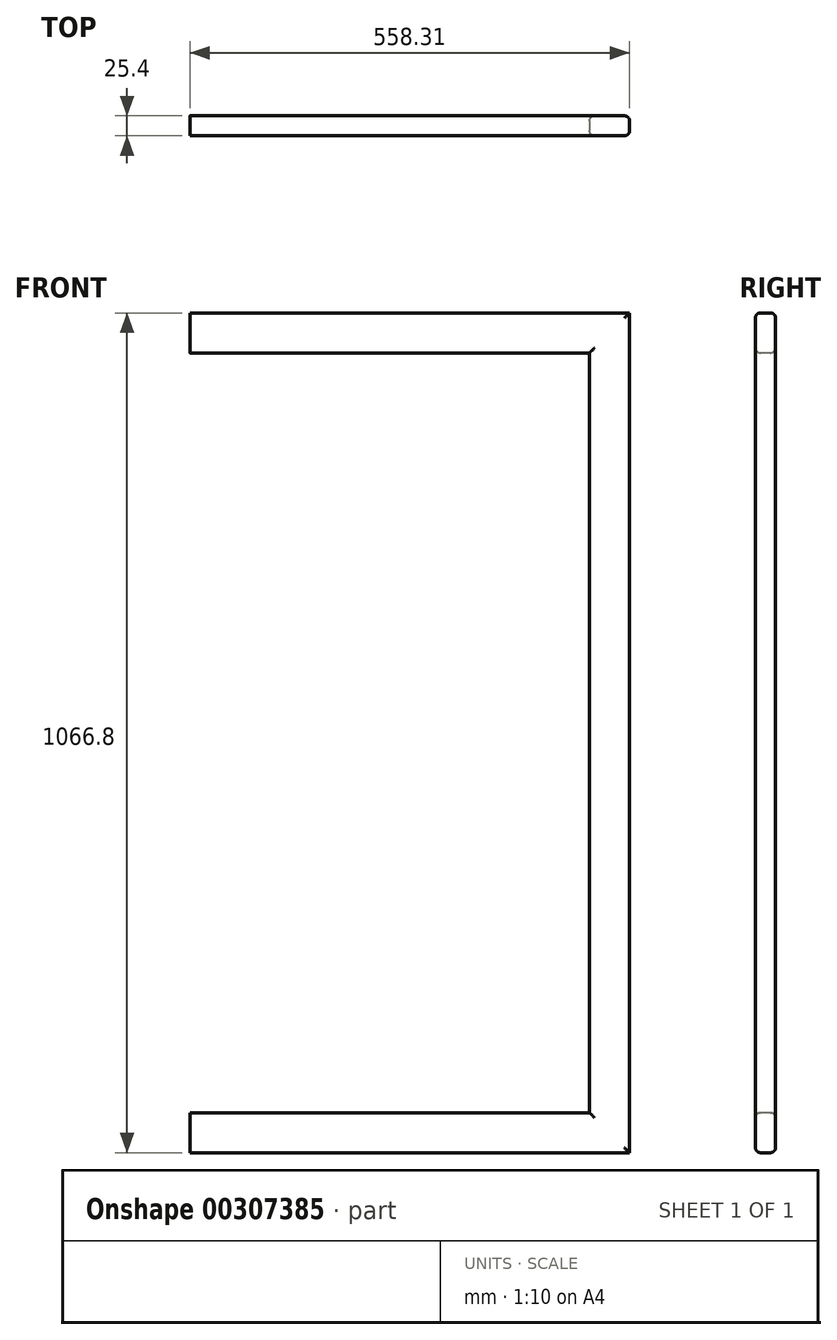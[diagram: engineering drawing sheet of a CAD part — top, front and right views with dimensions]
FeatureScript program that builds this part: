
annotation { "Feature Type Name" : "Feature", "Feature Type Description" : "" }
export const myFeature = defineFeature(function(context is Context, id is Id, definition is map)
    precondition{}
    {
        {
            var Q0;
            Q0=qCreatedBy(makeId("Front.planeOp"),FACE);
            var sketch = newSketch(context, id + "F0", { "sketchPlane" : qUnion([Q0])});
            skLineSegment(sketch, "E0", {"start": v(-2822.14, -1662.57) * mm, "end": v(-3065.65, 157.6) * mm});
            skLineSegment(sketch, "E1", {"start": v(-2797.6, -1589.77) * mm, "end": v(-3015.45, 102.14) * mm});
            skLineSegment(sketch, "E2", {"start": v(-3910.62, -1560.97) * mm, "end": v(-4015.94, -404.15) * mm});
            skLineSegment(sketch, "E3", {"start": v(-4015.94, -1560.97) * mm, "end": v(-4015.94, -404.15) * mm});
            skLineSegment(sketch, "E4", {"start": v(-4015.94, -404.15) * mm, "end": v(-4015.94, 15.92) * mm});
            skLineSegment(sketch, "E5", {"start": v(-3939.74, -1560.97) * mm, "end": v(-3939.74, -1310.71) * mm});
            skLineSegment(sketch, "E6", {"start": v(-4117.54, -1662.57) * mm, "end": v(-2823.92, -1662.57) * mm});
            skLineSegment(sketch, "E7", {"start": v(-4117.54, -1662.57) * mm, "end": v(-4117.54, 15.92) * mm});
            skLineSegment(sketch, "E8", {"start": v(-3895.3, -17.92) * mm, "end": v(-3895.3, -1662.57) * mm});
            skLineSegment(sketch, "E9", {"start": v(-3105.52, -1560.97) * mm, "end": v(-3491.84, -1560.97) * mm});
            skLineSegment(sketch, "E10", {"start": v(-2994.56, -1649.87) * mm, "end": v(-3096.16, -1649.87) * mm});
            skLineSegment(sketch, "E11", {"start": v(-2994.56, -1586.37) * mm, "end": v(-3096.16, -1586.37) * mm});
            skLineSegment(sketch, "E12", {"start": v(-4009.6, -1649.87) * mm, "end": v(-4111.2, -1649.87) * mm});
            skLineSegment(sketch, "E13", {"start": v(-4009.6, -1586.37) * mm, "end": v(-4111.2, -1586.37) * mm});
            skLineSegment(sketch, "E14", {"start": v(-4111.2, -1662.57) * mm, "end": v(-4111.2, -1586.37) * mm});
            skLineSegment(sketch, "E15", {"start": v(-4009.6, -1662.57) * mm, "end": v(-4009.6, -1586.37) * mm});
            skLineSegment(sketch, "E16", {"start": v(-2988.2, -1662.57) * mm, "end": v(-2988.2, -1560.97) * mm});
            skLineSegment(sketch, "E17", {"start": v(-2797.6, -1589.77) * mm, "end": v(-2823.92, -1662.57) * mm});
            skLineSegment(sketch, "E18", {"start": v(-4015.94, -1241.94) * mm, "end": v(-3953.21, -1241.94) * mm});
            skLineSegment(sketch, "E19", {"start": v(-2994.56, -1662.57) * mm, "end": v(-2994.56, -1586.37) * mm});
            skLineSegment(sketch, "E20", {"start": v(-3895.3, 217.03) * mm, "end": v(-3895.3, -17.92) * mm});
            skCircle(sketch, "E21", {"center": v(-4058.87, 166.23) * mm, "radius": 31.75 * mm});
            skCircle(sketch, "E22", {"center": v(-4058.87, 166.23) * mm, "radius": 26.92 * mm});
            skLineSegment(sketch, "E23", {"start": v(-3015.45, 102.14) * mm, "end": v(-3065.74, 157.9) * mm});
            skLineSegment(sketch, "E24", {"start": v(4405, 193.82) * mm, "end": v(3084.2, 193.82) * mm});
            skLineSegment(sketch, "E25", {"start": v(3085.2, -1658.86) * mm, "end": v(4405, -1658.86) * mm});
            skLineSegment(sketch, "E26", {"start": v(3084.2, -1654.29) * mm, "end": v(4405, -1654.29) * mm});
            skLineSegment(sketch, "E27", {"start": v(3004.35, -1658.98) * mm, "end": v(3004.35, 220.62) * mm});
            skLineSegment(sketch, "E28", {"start": v(3038.49, -1589.93) * mm, "end": v(3038.49, 154.88) * mm});
            skLineSegment(sketch, "E29", {"start": v(3041.54, -1586.18) * mm, "end": v(3041.54, 155.86) * mm});
            skLineSegment(sketch, "E30", {"start": v(3084.2, -1654.29) * mm, "end": v(3041.54, -1586.18) * mm});
            skLineSegment(sketch, "E31", {"start": v(3079.81, -1655.88) * mm, "end": v(3037.66, -1588.6) * mm});
            skLineSegment(sketch, "E32", {"start": v(2985.3, -1646.28) * mm, "end": v(2909.1, -1646.28) * mm});
            skArc(sketch, "E33", {"start": v(2909.1, -1646.28) * mm, "mid": v(2904.6, -1648.14) * mm, "end": v(2902.75, -1652.63) * mm});
            skLineSegment(sketch, "E34", {"start": v(2902.75, -1658.98) * mm, "end": v(2902.75, -1652.63) * mm});
            skLineSegment(sketch, "E35", {"start": v(3043.97, -1658.98) * mm, "end": v(3043.97, -1598.68) * mm});
            skLineSegment(sketch, "E36", {"start": v(3041.54, -1658.86) * mm, "end": v(3041.54, -1594.8) * mm});
            skLineSegment(sketch, "E37", {"start": v(3004.35, -1582.78) * mm, "end": v(2998, -1582.78) * mm});
            skLineSegment(sketch, "E38", {"start": v(2991.65, -1639.93) * mm, "end": v(2991.65, -1589.13) * mm});
            skArc(sketch, "E39", {"start": v(2998, -1582.78) * mm, "mid": v(2993.5, -1584.64) * mm, "end": v(2991.65, -1589.13) * mm});
            skArc(sketch, "E40", {"start": v(2985.3, -1646.28) * mm, "mid": v(2989.79, -1644.42) * mm, "end": v(2991.65, -1639.93) * mm});
            skLineSegment(sketch, "E41", {"start": v(3043.97, -1617.83) * mm, "end": v(3055.97, -1617.83) * mm});
            skLineSegment(sketch, "E42", {"start": v(3038.49, -1586.18) * mm, "end": v(3041.54, -1586.18) * mm});
            skArc(sketch, "E43", {"start": v(3079.81, -1655.88) * mm, "mid": v(3082.12, -1658.07) * mm, "end": v(3085.2, -1658.86) * mm});
            skLineSegment(sketch, "E44", {"start": v(3068.03, 201.69) * mm, "end": v(3046.1, 201.69) * mm});
            skLineSegment(sketch, "E45", {"start": v(3084.2, 220.74) * mm, "end": v(3041.54, 155.86) * mm});
            skLineSegment(sketch, "E46", {"start": v(3081.66, 222.41) * mm, "end": v(3039.53, 158.37) * mm});
            skLineSegment(sketch, "E47", {"start": v(3007.4, 220.62) * mm, "end": v(3007.4, 223.92) * mm});
            skLineSegment(sketch, "E48", {"start": v(3047.27, 170.13) * mm, "end": v(3047.27, 220.62) * mm});
            skLineSegment(sketch, "E49", {"start": v(3043.97, 220.62) * mm, "end": v(3043.97, 166.3) * mm});
            skArc(sketch, "E50", {"start": v(3039.53, 158.37) * mm, "mid": v(3038.75, 156.7) * mm, "end": v(3038.49, 154.88) * mm});
            skLineSegment(sketch, "E51", {"start": v(3007.4, 223.92) * mm, "end": v(3043.97, 223.92) * mm});
            skLineSegment(sketch, "E52", {"start": v(3004.35, 220.62) * mm, "end": v(3043.97, 220.62) * mm});
            skArc(sketch, "E53", {"start": v(3047.27, 220.62) * mm, "mid": v(3046.3, 222.96) * mm, "end": v(3043.97, 223.92) * mm});
            skLineSegment(sketch, "E54", {"start": v(4409.58, 220.74) * mm, "end": v(3079.64, 220.74) * mm});
            skLineSegment(sketch, "E55", {"start": v(4490, -1658.98) * mm, "end": v(4490, 220.62) * mm});
            skLineSegment(sketch, "E56", {"start": v(4405, -1658.86) * mm, "end": v(4405, 352.31) * mm});
            skLineSegment(sketch, "E57", {"start": v(4447.68, -1586.18) * mm, "end": v(4447.68, 155.86) * mm});
            skLineSegment(sketch, "E58", {"start": v(4450.73, -1589.93) * mm, "end": v(4450.73, 154.88) * mm});
            skLineSegment(sketch, "E59", {"start": v(4409.4, -1655.88) * mm, "end": v(4451.55, -1588.6) * mm});
            skLineSegment(sketch, "E60", {"start": v(4405, -1654.29) * mm, "end": v(4447.68, -1586.18) * mm});
            skLineSegment(sketch, "E61", {"start": v(4447.68, -1658.86) * mm, "end": v(4447.68, -1594.8) * mm});
            skLineSegment(sketch, "E62", {"start": v(4445.24, -1658.98) * mm, "end": v(4445.24, -1598.68) * mm});
            skArc(sketch, "E63", {"start": v(4404.02, -1658.86) * mm, "mid": v(4407.1, -1658.07) * mm, "end": v(4409.4, -1655.88) * mm});
            skLineSegment(sketch, "E64", {"start": v(4450.73, -1586.18) * mm, "end": v(4447.68, -1586.18) * mm});
            skLineSegment(sketch, "E65", {"start": v(4445.24, -1617.83) * mm, "end": v(4433.25, -1617.83) * mm});
            skLineSegment(sketch, "E66", {"start": v(4556.6, -1692.31) * mm, "end": v(4620.6, -1806.17) * mm});
            skArc(sketch, "E67", {"start": v(4588.54, -1652.63) * mm, "mid": v(4586.68, -1648.14) * mm, "end": v(4582.2, -1646.28) * mm});
            skLineSegment(sketch, "E68", {"start": v(4506, -1646.28) * mm, "end": v(4582.2, -1646.28) * mm});
            skArc(sketch, "E69", {"start": v(4499.64, -1639.93) * mm, "mid": v(4501.5, -1644.42) * mm, "end": v(4506, -1646.28) * mm});
            skArc(sketch, "E70", {"start": v(4499.64, -1589.13) * mm, "mid": v(4497.78, -1584.64) * mm, "end": v(4493.3, -1582.78) * mm});
            skLineSegment(sketch, "E71", {"start": v(4499.64, -1639.93) * mm, "end": v(4499.64, -1589.13) * mm});
            skLineSegment(sketch, "E72", {"start": v(4486.94, -1582.78) * mm, "end": v(4493.3, -1582.78) * mm});
            skLineSegment(sketch, "E73", {"start": v(4588.54, -1658.98) * mm, "end": v(4588.54, -1652.63) * mm});
            skLineSegment(sketch, "E74", {"start": v(4490, 220.62) * mm, "end": v(4447.32, 220.62) * mm});
            skLineSegment(sketch, "E75", {"start": v(4486.94, 223.92) * mm, "end": v(4447.07, 223.92) * mm});
            skLineSegment(sketch, "E76", {"start": v(4445.24, 220.62) * mm, "end": v(4445.24, 166.3) * mm});
            skLineSegment(sketch, "E77", {"start": v(4407.55, 222.41) * mm, "end": v(4449.68, 158.37) * mm});
            skLineSegment(sketch, "E78", {"start": v(4405, 220.74) * mm, "end": v(4447.68, 155.86) * mm});
            skLineSegment(sketch, "E79", {"start": v(4441.94, 170.13) * mm, "end": v(4441.94, 220.62) * mm});
            skArc(sketch, "E80", {"start": v(4450.73, 154.88) * mm, "mid": v(4450.46, 156.7) * mm, "end": v(4449.68, 158.37) * mm});
            skLineSegment(sketch, "E81", {"start": v(4421.19, 201.69) * mm, "end": v(4443.1, 201.69) * mm});
            skArc(sketch, "E82", {"start": v(4445.24, 223.92) * mm, "mid": v(4442.9, 222.96) * mm, "end": v(4441.94, 220.62) * mm});
            skLineSegment(sketch, "E83", {"start": v(4486.94, 220.62) * mm, "end": v(4486.94, 223.92) * mm});
            skLineSegment(sketch, "E84", {"start": v(1268.38, 2115.98) * mm, "end": v(1268.38, 2338.23) * mm});
            skLineSegment(sketch, "E85", {"start": v(4.47, 2115.98) * mm, "end": v(4.47, 2338.23) * mm});
            skLineSegment(sketch, "E86", {"start": v(1391.64, 1119.03) * mm, "end": v(1391.64, 2338.23) * mm});
            skLineSegment(sketch, "E87", {"start": v(1349.33, 1119.03) * mm, "end": v(1349.33, 2338.23) * mm});
            skLineSegment(sketch, "E88", {"start": v(-36.67, 2115.98) * mm, "end": v(1309.53, 2115.98) * mm});
            skLineSegment(sketch, "E89", {"start": v(-76.48, 1119.03) * mm, "end": v(-76.48, 2338.23) * mm});
            skLineSegment(sketch, "E90", {"start": v(-119.4, 1119.03) * mm, "end": v(-119.4, 2338.23) * mm});
            skLineSegment(sketch, "E91", {"start": v(1309.53, 985.68) * mm, "end": v(1309.53, 2338.23) * mm});
            skLineSegment(sketch, "E92", {"start": v(-36.67, 985.68) * mm, "end": v(-36.67, 2338.23) * mm});
            skLineSegment(sketch, "E93", {"start": v(-36.67, 985.68) * mm, "end": v(1309.53, 985.68) * mm});
            skLineSegment(sketch, "E94", {"start": v(-132.1, 1125.38) * mm, "end": v(-132.1, 1226.98) * mm});
            skLineSegment(sketch, "E95", {"start": v(-119.4, 1119.03) * mm, "end": v(-76.48, 1119.03) * mm});
            skLineSegment(sketch, "E96", {"start": v(-119.4, 1125.38) * mm, "end": v(-221, 1125.38) * mm});
            skCircle(sketch, "E97", {"center": v(-176.55, 1176.18) * mm, "radius": 6.86 * mm});
            skLineSegment(sketch, "E98", {"start": v(-221, 1226.98) * mm, "end": v(-119.4, 1226.98) * mm});
            skLineSegment(sketch, "E99", {"start": v(1349.33, 1119.03) * mm, "end": v(1391.64, 1119.03) * mm});
            skLineSegment(sketch, "E100", {"start": v(-75.54, 2255.68) * mm, "end": v(-75.54, 2319.18) * mm});
            skLineSegment(sketch, "E101", {"start": v(43.34, 2255.68) * mm, "end": v(43.34, 2319.18) * mm});
            skLineSegment(sketch, "E102", {"start": v(1268.38, 2236.63) * mm, "end": v(4.47, 2236.63) * mm});
            skLineSegment(sketch, "E103", {"start": v(43.34, 2262.03) * mm, "end": v(1229.52, 2262.03) * mm});
            skLineSegment(sketch, "E104", {"start": v(43.34, 2312.83) * mm, "end": v(1229.52, 2312.83) * mm});
            skLineSegment(sketch, "E105", {"start": v(-75.54, 2262.03) * mm, "end": v(-115.6, 2262.03) * mm});
            skLineSegment(sketch, "E106", {"start": v(-119.4, 2338.23) * mm, "end": v(1391.64, 2338.23) * mm});
            skArc(sketch, "E107", {"start": v(-115.6, 2250.19) * mm, "mid": v(-114.23, 2246.25) * mm, "end": v(-110.72, 2244.01) * mm});
            skLineSegment(sketch, "E108", {"start": v(-115.6, 2250.26) * mm, "end": v(-115.6, 2324.68) * mm});
            skLineSegment(sketch, "E109", {"start": v(-78.26, 2240.44) * mm, "end": v(-110.72, 2244.01) * mm});
            skLineSegment(sketch, "E110", {"start": v(-119.4, 2236.63) * mm, "end": v(-36.67, 2236.63) * mm});
            skLineSegment(sketch, "E111", {"start": v(-36.67, 2255.68) * mm, "end": v(-75.54, 2255.68) * mm});
            skLineSegment(sketch, "E112", {"start": v(43.34, 2255.68) * mm, "end": v(4.47, 2255.68) * mm});
            skLineSegment(sketch, "E113", {"start": v(-75.54, 2312.83) * mm, "end": v(-115.6, 2312.83) * mm});
            skLineSegment(sketch, "E114", {"start": v(-78.26, 2334.42) * mm, "end": v(-110.72, 2330.86) * mm});
            skLineSegment(sketch, "E115", {"start": v(-78.26, 2338.23) * mm, "end": v(-119.4, 2338.23) * mm});
            skArc(sketch, "E116", {"start": v(-110.72, 2330.86) * mm, "mid": v(-114.23, 2328.62) * mm, "end": v(-115.6, 2324.68) * mm});
            skLineSegment(sketch, "E117", {"start": v(-36.67, 2319.18) * mm, "end": v(-75.54, 2319.18) * mm});
            skLineSegment(sketch, "E118", {"start": v(43.34, 2319.18) * mm, "end": v(4.47, 2319.18) * mm});
            skLineSegment(sketch, "E119", {"start": v(1348.39, 2262.03) * mm, "end": v(1388.44, 2262.03) * mm});
            skLineSegment(sketch, "E120", {"start": v(1348.39, 2312.83) * mm, "end": v(1388.44, 2312.83) * mm});
            skLineSegment(sketch, "E121", {"start": v(1349.33, 2236.63) * mm, "end": v(1391.64, 2236.63) * mm});
            skLineSegment(sketch, "E122", {"start": v(1351.1, 2240.44) * mm, "end": v(1383.57, 2244.01) * mm});
            skLineSegment(sketch, "E123", {"start": v(1351.1, 2334.42) * mm, "end": v(1383.57, 2330.86) * mm});
            skLineSegment(sketch, "E124", {"start": v(1348.39, 2255.68) * mm, "end": v(1348.39, 2319.18) * mm});
            skLineSegment(sketch, "E125", {"start": v(1229.52, 2255.68) * mm, "end": v(1229.52, 2319.18) * mm});
            skLineSegment(sketch, "E126", {"start": v(1229.52, 2255.68) * mm, "end": v(1268.38, 2255.68) * mm});
            skLineSegment(sketch, "E127", {"start": v(1349.33, 2236.63) * mm, "end": v(1309.53, 2236.63) * mm});
            skLineSegment(sketch, "E128", {"start": v(1309.53, 2255.68) * mm, "end": v(1348.39, 2255.68) * mm});
            skLineSegment(sketch, "E129", {"start": v(1229.52, 2319.18) * mm, "end": v(1268.38, 2319.18) * mm});
            skLineSegment(sketch, "E130", {"start": v(1309.53, 2319.18) * mm, "end": v(1348.39, 2319.18) * mm});
            skLineSegment(sketch, "E131", {"start": v(1388.44, 2250.26) * mm, "end": v(1388.44, 2324.68) * mm});
            skArc(sketch, "E132", {"start": v(1383.57, 2244.01) * mm, "mid": v(1387.08, 2246.25) * mm, "end": v(1388.44, 2250.19) * mm});
            skArc(sketch, "E133", {"start": v(1388.44, 2324.68) * mm, "mid": v(1387.08, 2328.62) * mm, "end": v(1383.57, 2330.86) * mm});
            skLineSegment(sketch, "E134", {"start": v(1467.84, 2325.63) * mm, "end": v(1467.84, 2224.03) * mm});
            skLineSegment(sketch, "E135", {"start": v(1404.34, 2325.63) * mm, "end": v(1404.34, 2224.03) * mm});
            skLineSegment(sketch, "E136", {"start": v(1391.64, 2224.03) * mm, "end": v(1391.64, 2325.63) * mm});
            skLineSegment(sketch, "E137", {"start": v(1391.64, 2325.63) * mm, "end": v(1467.84, 2325.63) * mm});
            skLineSegment(sketch, "E138", {"start": v(-123.35, 2335.19) * mm, "end": v(-123.35, 2125.64) * mm});
            skCircle(sketch, "E139", {"center": v(1436.1, 2274.83) * mm, "radius": 6.86 * mm});
            skLineSegment(sketch, "E140", {"start": v(1467.84, 2224.03) * mm, "end": v(1391.64, 2224.03) * mm});
            skLineSegment(sketch, "E141", {"start": v(-221, 1226.98) * mm, "end": v(-221, 1125.38) * mm});
            skLineSegment(sketch, "E142", {"start": v(1392.25, 1226.98) * mm, "end": v(1392.25, 1125.38) * mm});
            skLineSegment(sketch, "E143", {"start": v(1404.95, 1125.38) * mm, "end": v(1404.95, 1226.98) * mm});
            skLineSegment(sketch, "E144", {"start": v(1493.85, 1125.38) * mm, "end": v(1493.85, 1226.98) * mm});
            skLineSegment(sketch, "E145", {"start": v(1392.25, 1125.38) * mm, "end": v(1493.85, 1125.38) * mm});
            skCircle(sketch, "E146", {"center": v(1449.4, 1176.18) * mm, "radius": 6.86 * mm});
            skLineSegment(sketch, "E147", {"start": v(1493.85, 1226.98) * mm, "end": v(1392.25, 1226.98) * mm});
            skLineSegment(sketch, "E148", {"start": v(1493.85, 1226.98) * mm, "end": v(1493.85, 1125.38) * mm});
            skLineSegment(sketch, "E149", {"start": v(3084.2, 352.31) * mm, "end": v(4405, 352.31) * mm});
            skLineSegment(sketch, "E150", {"start": v(3084.2, -1658.86) * mm, "end": v(3084.2, 352.31) * mm});
            skLineSegment(sketch, "E151", {"start": v(-3930.07, 217.03) * mm, "end": v(-3983.26, 217.03) * mm});
            skLineSegment(sketch, "E152", {"start": v(-3895.3, 344.03) * mm, "end": v(-3895.3, 217.03) * mm});
            skLineSegment(sketch, "E153", {"start": v(-3890.72, 344.03) * mm, "end": v(-3415.64, 344.03) * mm});
            skLineSegment(sketch, "E154", {"start": v(-3083.2, 214.13) * mm, "end": v(-3308.19, 344.03) * mm});
            skLineSegment(sketch, "E155", {"start": v(-3083.2, 214.13) * mm, "end": v(-3065.65, 157.6) * mm});
            skLineSegment(sketch, "E156", {"start": v(-36.67, 1223.6) * mm, "end": v(-72.6, 1187.67) * mm});
            skLineSegment(sketch, "E157", {"start": v(-72.6, 1187.67) * mm, "end": v(-72.6, 1004.21) * mm});
            skLineSegment(sketch, "E158", {"start": v(-72.6, 1004.21) * mm, "end": v(-36.67, 985.68) * mm});
            skLineSegment(sketch, "E159", {"start": v(1309.53, 1223.6) * mm, "end": v(1345.45, 1187.67) * mm});
            skLineSegment(sketch, "E160", {"start": v(1345.45, 1187.67) * mm, "end": v(1345.45, 1004.21) * mm});
            skLineSegment(sketch, "E161", {"start": v(1345.45, 1004.21) * mm, "end": v(1309.53, 985.68) * mm});
            skArc(sketch, "E162", {"start": v(-2823.92, -1662.57) * mm, "mid": v(-1901.54, 614.6) * mm, "end": v(-3652.4, 2338.2) * mm});
            skCircle(sketch, "E163", {"center": v(-3126.94, 115.43) * mm, "radius": 7.5 * mm});
            skCircle(sketch, "E164", {"center": v(-3126.94, 64.63) * mm, "radius": 7.5 * mm});
            skCircle(sketch, "E165", {"center": v(-3126.94, 13.83) * mm, "radius": 7.5 * mm});
            skCircle(sketch, "E166", {"center": v(-3126.94, -36.97) * mm, "radius": 7.5 * mm});
            skCircle(sketch, "E167", {"center": v(-3126.94, -87.77) * mm, "radius": 7.5 * mm});
            skCircle(sketch, "E168", {"center": v(-3126.94, -240.17) * mm, "radius": 7.5 * mm});
            skCircle(sketch, "E169", {"center": v(-3126.94, -189.37) * mm, "radius": 7.5 * mm});
            skCircle(sketch, "E170", {"center": v(-3126.94, -138.57) * mm, "radius": 7.5 * mm});
            skLineSegment(sketch, "E171", {"start": v(-123.35, 2335.19) * mm, "end": v(-123.35, 1823.88) * mm});
            skLineSegment(sketch, "E172", {"start": v(-123.35, 2125.64) * mm, "end": v(-119.4, 2125.64) * mm});
            skLineSegment(sketch, "E173", {"start": v(-123.35, 2335.19) * mm, "end": v(-119.4, 2335.19) * mm});
            skLineSegment(sketch, "E174", {"start": v(-197.73, -345.12) * mm, "end": v(-273.93, -345.12) * mm});
            skArc(sketch, "E175", {"start": v(-273.93, -345.12) * mm, "mid": v(-276.27, -344.16) * mm, "end": v(-277.23, -341.82) * mm});
            skLineSegment(sketch, "E176", {"start": v(-277.23, -341.82) * mm, "end": v(-277.23, -265.62) * mm});
            skArc(sketch, "E177", {"start": v(-277.23, -265.62) * mm, "mid": v(-276.27, -263.29) * mm, "end": v(-273.93, -262.32) * mm});
            skLineSegment(sketch, "E178", {"start": v(-273.93, -262.32) * mm, "end": v(-197.73, -262.32) * mm});
            skLineSegment(sketch, "E179", {"start": v(-197.73, -262.32) * mm, "end": v(-197.73, -265.62) * mm});
            skLineSegment(sketch, "E180", {"start": v(-197.73, -265.62) * mm, "end": v(-273.93, -265.62) * mm});
            skLineSegment(sketch, "E181", {"start": v(-273.93, -265.62) * mm, "end": v(-273.93, -341.82) * mm});
            skLineSegment(sketch, "E182", {"start": v(-273.93, -341.82) * mm, "end": v(-197.73, -341.82) * mm});
            skLineSegment(sketch, "E183", {"start": v(-197.73, -341.82) * mm, "end": v(-197.73, -345.12) * mm});
            skLineSegment(sketch, "E184", {"start": v(-175.63, -341.82) * mm, "end": v(-175.63, -265.62) * mm});
            skArc(sketch, "E185", {"start": v(-175.63, -265.62) * mm, "mid": v(-177.5, -261.13) * mm, "end": v(-181.98, -259.27) * mm});
            skLineSegment(sketch, "E186", {"start": v(-181.98, -259.27) * mm, "end": v(-328.03, -259.27) * mm});
            skArc(sketch, "E187", {"start": v(-328.03, -259.27) * mm, "mid": v(-332.52, -261.13) * mm, "end": v(-334.38, -265.62) * mm});
            skLineSegment(sketch, "E188", {"start": v(-334.38, -265.62) * mm, "end": v(-334.38, -341.82) * mm});
            skCircle(sketch, "E189", {"center": v(-197.86, -303.72) * mm, "radius": 7.11 * mm});
            skCircle(sketch, "E190", {"center": v(-312.16, -303.72) * mm, "radius": 7.11 * mm});
            skArc(sketch, "E191", {"start": v(-181.98, -348.17) * mm, "mid": v(-177.5, -346.31) * mm, "end": v(-175.63, -341.82) * mm});
            skLineSegment(sketch, "E192", {"start": v(-181.98, -348.17) * mm, "end": v(-328.03, -348.17) * mm});
            skArc(sketch, "E193", {"start": v(-334.38, -341.82) * mm, "mid": v(-332.52, -346.31) * mm, "end": v(-328.03, -348.17) * mm});
            skLineSegment(sketch, "E194", {"start": v(-223.13, -262.32) * mm, "end": v(-197.73, -262.32) * mm});
            skLineSegment(sketch, "E195", {"start": v(-197.73, -262.32) * mm, "end": v(-197.73, 1820.48) * mm});
            skLineSegment(sketch, "E196", {"start": v(-197.73, 1820.48) * mm, "end": v(-223.13, 1820.48) * mm});
            skLineSegment(sketch, "E197", {"start": v(-223.13, 1820.48) * mm, "end": v(-223.13, -262.32) * mm});
            skLineSegment(sketch, "E198", {"start": v(-223.13, 1823.88) * mm, "end": v(-123.35, 1823.88) * mm});
            skLineSegment(sketch, "E199", {"start": v(-197.73, 1820.48) * mm, "end": v(-119.4, 1820.48) * mm});
            skLineSegment(sketch, "E200", {"start": v(1469.97, -345.12) * mm, "end": v(1546.17, -345.12) * mm});
            skArc(sketch, "E201", {"start": v(1546.17, -345.12) * mm, "mid": v(1548.5, -344.16) * mm, "end": v(1549.47, -341.82) * mm});
            skLineSegment(sketch, "E202", {"start": v(1549.47, -341.82) * mm, "end": v(1549.47, -265.62) * mm});
            skArc(sketch, "E203", {"start": v(1549.47, -265.62) * mm, "mid": v(1548.5, -263.29) * mm, "end": v(1546.17, -262.32) * mm});
            skLineSegment(sketch, "E204", {"start": v(1546.17, -262.32) * mm, "end": v(1469.97, -262.32) * mm});
            skLineSegment(sketch, "E205", {"start": v(1469.97, -262.32) * mm, "end": v(1469.97, -265.62) * mm});
            skLineSegment(sketch, "E206", {"start": v(1469.97, -265.62) * mm, "end": v(1546.17, -265.62) * mm});
            skLineSegment(sketch, "E207", {"start": v(1546.17, -265.62) * mm, "end": v(1546.17, -341.82) * mm});
            skLineSegment(sketch, "E208", {"start": v(1546.17, -341.82) * mm, "end": v(1469.97, -341.82) * mm});
            skLineSegment(sketch, "E209", {"start": v(1469.97, -341.82) * mm, "end": v(1469.97, -345.12) * mm});
            skLineSegment(sketch, "E210", {"start": v(1447.87, -341.82) * mm, "end": v(1447.87, -265.62) * mm});
            skArc(sketch, "E211", {"start": v(1454.22, -259.27) * mm, "mid": v(1449.73, -261.13) * mm, "end": v(1447.87, -265.62) * mm});
            skLineSegment(sketch, "E212", {"start": v(1454.22, -259.27) * mm, "end": v(1600.27, -259.27) * mm});
            skArc(sketch, "E213", {"start": v(1606.62, -265.62) * mm, "mid": v(1604.76, -261.13) * mm, "end": v(1600.27, -259.27) * mm});
            skLineSegment(sketch, "E214", {"start": v(1606.62, -265.62) * mm, "end": v(1606.62, -341.82) * mm});
            skCircle(sketch, "E215", {"center": v(1470.1, -303.72) * mm, "radius": 7.11 * mm});
            skCircle(sketch, "E216", {"center": v(1584.4, -303.72) * mm, "radius": 7.11 * mm});
            skArc(sketch, "E217", {"start": v(1447.87, -341.82) * mm, "mid": v(1449.73, -346.31) * mm, "end": v(1454.22, -348.17) * mm});
            skLineSegment(sketch, "E218", {"start": v(1454.22, -348.17) * mm, "end": v(1600.27, -348.17) * mm});
            skArc(sketch, "E219", {"start": v(1600.27, -348.17) * mm, "mid": v(1604.76, -346.31) * mm, "end": v(1606.62, -341.82) * mm});
            skLineSegment(sketch, "E220", {"start": v(1495.37, -262.32) * mm, "end": v(1469.97, -262.32) * mm});
            skLineSegment(sketch, "E221", {"start": v(1469.97, -262.32) * mm, "end": v(1469.97, 1820.48) * mm});
            skLineSegment(sketch, "E222", {"start": v(1469.97, 1820.48) * mm, "end": v(1495.37, 1820.48) * mm});
            skLineSegment(sketch, "E223", {"start": v(1495.37, 1820.48) * mm, "end": v(1495.37, -262.32) * mm});
            skLineSegment(sketch, "E224", {"start": v(1495.37, 1823.88) * mm, "end": v(1393.77, 1823.88) * mm});
            skLineSegment(sketch, "E225", {"start": v(1469.97, 1820.48) * mm, "end": v(1391.64, 1820.48) * mm});
            skLineSegment(sketch, "E226", {"start": v(1393.77, 1823.88) * mm, "end": v(1393.77, 2338.23) * mm});
            skLineSegment(sketch, "E227", {"start": v(-191.66, -345.12) * mm, "end": v(1466.92, -345.12) * mm});
            skLineSegment(sketch, "E228", {"start": v(1466.92, -345.12) * mm, "end": v(1466.92, -319.72) * mm});
            skLineSegment(sketch, "E229", {"start": v(1466.92, -319.72) * mm, "end": v(-191.66, -319.72) * mm});
            skLineSegment(sketch, "E230", {"start": v(-191.66, -319.72) * mm, "end": v(-191.66, -345.12) * mm});
            skLineSegment(sketch, "E231", {"start": v(1469.97, -1981.35) * mm, "end": v(1469.97, -348.17) * mm});
            skLineSegment(sketch, "E232", {"start": v(1469.97, -348.17) * mm, "end": v(1495.37, -348.17) * mm});
            skLineSegment(sketch, "E233", {"start": v(1495.37, -348.17) * mm, "end": v(1495.37, -1981.35) * mm});
            skLineSegment(sketch, "E234", {"start": v(1495.37, -1981.35) * mm, "end": v(1469.97, -1981.35) * mm});
            skArc(sketch, "E235", {"start": v(-191.4, -319.72) * mm, "mid": v(289.32, -1500.37) * mm, "end": v(1469.97, -1981.1) * mm});
            skLineSegment(sketch, "E236", {"start": v(-195.6, 2325.63) * mm, "end": v(-195.6, 2224.03) * mm});
            skLineSegment(sketch, "E237", {"start": v(-132.1, 2325.63) * mm, "end": v(-132.1, 2224.03) * mm});
            skLineSegment(sketch, "E238", {"start": v(-119.4, 2325.63) * mm, "end": v(-195.6, 2325.63) * mm});
            skCircle(sketch, "E239", {"center": v(-163.85, 2274.83) * mm, "radius": 6.86 * mm});
            skLineSegment(sketch, "E240", {"start": v(-195.6, 2224.03) * mm, "end": v(-119.4, 2224.03) * mm});
            skLineSegment(sketch, "E241", {"start": v(-4123.95, 237.68) * mm, "end": v(-3991.34, 237.68) * mm});
            skLineSegment(sketch, "E242", {"start": v(-4130.3, -17.93) * mm, "end": v(-4130.3, 231.33) * mm});
            skArc(sketch, "E243", {"start": v(-4123.95, 237.68) * mm, "mid": v(-4128.44, 235.82) * mm, "end": v(-4130.3, 231.33) * mm});
            skArc(sketch, "E244", {"start": v(-3985.47, 233.74) * mm, "mid": v(-3987.8, 236.6) * mm, "end": v(-3991.34, 237.68) * mm});
            skCircle(sketch, "E245", {"center": v(-4003.3, 110.67) * mm, "radius": 7.5 * mm});
            skCircle(sketch, "E246", {"center": v(-4003.3, 221.8) * mm, "radius": 7.5 * mm});
            skCircle(sketch, "E247", {"center": v(-4114.43, 110.67) * mm, "radius": 7.5 * mm});
            skCircle(sketch, "E248", {"center": v(-4114.43, 221.8) * mm, "radius": 7.5 * mm});
            skLineSegment(sketch, "E249", {"start": v(-3096.16, -1586.37) * mm, "end": v(-3096.16, -1662.57) * mm});
            skLineSegment(sketch, "E250", {"start": v(-4123.95, -24.28) * mm, "end": v(-4117.54, -24.28) * mm});
            skLineSegment(sketch, "E251", {"start": v(-3105.52, -1560.97) * mm, "end": v(-3492.42, -890.84) * mm});
            skLineSegment(sketch, "E252", {"start": v(-4015.94, 15.92) * mm, "end": v(-4117.54, 15.92) * mm});
            skLineSegment(sketch, "E253", {"start": v(-2988.2, -1560.97) * mm, "end": v(-3491.84, -688.65) * mm});
            skLineSegment(sketch, "E254", {"start": v(-3898.62, 15.92) * mm, "end": v(-3947.92, 101.3) * mm});
            skLineSegment(sketch, "E255", {"start": v(-3985.47, 166.34) * mm, "end": v(-3985.47, 233.74) * mm});
            skLineSegment(sketch, "E256", {"start": v(-4015.94, 15.92) * mm, "end": v(-3927.95, 66.72) * mm});
            skArc(sketch, "E257", {"start": v(-4130.3, -17.93) * mm, "mid": v(-4128.44, -22.42) * mm, "end": v(-4123.95, -24.28) * mm});
            skLineSegment(sketch, "E258", {"start": v(-4117.54, -1662.57) * mm, "end": v(-4117.54, 91.62) * mm});
            skLineSegment(sketch, "E259", {"start": v(-3947.92, 101.3) * mm, "end": v(-3985.47, 166.34) * mm});
            skLineSegment(sketch, "E260", {"start": v(-3523.43, -837.13) * mm, "end": v(-4015.94, 15.92) * mm});
            skLineSegment(sketch, "E261", {"start": v(-3513.28, -651.52) * mm, "end": v(-3898.62, 15.92) * mm});
            skLineSegment(sketch, "E262", {"start": v(-3520.24, -1560.97) * mm, "end": v(-4015.94, -1560.97) * mm});
            skCircle(sketch, "E263", {"center": v(-3126.94, -36.97) * mm, "radius": 5.2 * mm});
            skCircle(sketch, "E264", {"center": v(-3126.94, 13.83) * mm, "radius": 5.2 * mm});
            skLineSegment(sketch, "E265", {"start": v(-3165.04, 20.18) * mm, "end": v(-3165.04, -94.12) * mm});
            skArc(sketch, "E266", {"start": v(-3152.34, 32.88) * mm, "mid": v(-3161.32, 29.16) * mm, "end": v(-3165.04, 20.18) * mm});
            skArc(sketch, "E267", {"start": v(-3101.54, -106.82) * mm, "mid": v(-3092.56, -103.1) * mm, "end": v(-3088.84, -94.12) * mm});
            skLineSegment(sketch, "E268", {"start": v(-3101.54, 32.88) * mm, "end": v(-3152.34, 32.88) * mm});
            skArc(sketch, "E269", {"start": v(-3088.84, 20.18) * mm, "mid": v(-3092.56, 29.16) * mm, "end": v(-3101.54, 32.88) * mm});
            skLineSegment(sketch, "E270", {"start": v(-3101.54, -106.82) * mm, "end": v(-3152.34, -106.82) * mm});
            skArc(sketch, "E271", {"start": v(-3165.04, -94.12) * mm, "mid": v(-3161.32, -103.1) * mm, "end": v(-3152.34, -106.82) * mm});
            skCircle(sketch, "E272", {"center": v(-3126.94, -36.97) * mm, "radius": 9.65 * mm});
            skCircle(sketch, "E273", {"center": v(-3126.94, -87.77) * mm, "radius": 5.2 * mm});
            skLineSegment(sketch, "E274", {"start": v(-3088.84, 20.18) * mm, "end": v(-3088.84, -94.12) * mm});
            skCircle(sketch, "E275", {"center": v(-3096.75, 200.66) * mm, "radius": 13.46 * mm});
            skCircle(sketch, "E276", {"center": v(-3096.75, 200.66) * mm, "radius": 5.33 * mm});
            skLineSegment(sketch, "E277", {"start": v(-4017.51, 115.7) * mm, "end": v(-3054.4, -142.36) * mm});
            skLineSegment(sketch, "E278", {"start": v(-4067.68, 133.36) * mm, "end": v(-3055.61, -137.82) * mm});
            skLineSegment(sketch, "E279", {"start": v(-4001.93, 190.42) * mm, "end": v(-3077.17, -57.37) * mm});
            skLineSegment(sketch, "E280", {"start": v(-4050.06, 199.1) * mm, "end": v(-3075.95, -61.9) * mm});
            skLineSegment(sketch, "E281", {"start": v(-3054.4, -142.36) * mm, "end": v(-3077.17, -57.37) * mm});
            skCircle(sketch, "E282", {"center": v(-4058.87, 166.23) * mm, "radius": 25.4 * mm});
            skCircle(sketch, "E283", {"center": v(3338.2, -24.76) * mm, "radius": 5.2 * mm});
            skCircle(sketch, "E284", {"center": v(3338.2, 26.04) * mm, "radius": 5.2 * mm});
            skCircle(sketch, "E285", {"center": v(3338.2, 127.64) * mm, "radius": 5.2 * mm});
            skCircle(sketch, "E286", {"center": v(3338.2, 76.84) * mm, "radius": 5.2 * mm});
            skLineSegment(sketch, "E287", {"start": v(3300.1, 32.2) * mm, "end": v(3300.1, -82.1) * mm});
            skArc(sketch, "E288", {"start": v(3312.8, 44.9) * mm, "mid": v(3303.83, 41.17) * mm, "end": v(3300.1, 32.2) * mm});
            skArc(sketch, "E289", {"start": v(3363.6, -94.8) * mm, "mid": v(3372.59, -91.09) * mm, "end": v(3376.3, -82.1) * mm});
            skLineSegment(sketch, "E290", {"start": v(3363.6, 44.9) * mm, "end": v(3312.8, 44.9) * mm});
            skArc(sketch, "E291", {"start": v(3376.3, 32.2) * mm, "mid": v(3372.59, 41.17) * mm, "end": v(3363.6, 44.9) * mm});
            skLineSegment(sketch, "E292", {"start": v(3363.6, -94.8) * mm, "end": v(3312.8, -94.8) * mm});
            skArc(sketch, "E293", {"start": v(3300.1, -82.1) * mm, "mid": v(3303.83, -91.09) * mm, "end": v(3312.8, -94.8) * mm});
            skCircle(sketch, "E294", {"center": v(3338.2, -24.96) * mm, "radius": 9.65 * mm});
            skCircle(sketch, "E295", {"center": v(3338.2, -126.36) * mm, "radius": 5.2 * mm});
            skCircle(sketch, "E296", {"center": v(3338.2, -75.56) * mm, "radius": 5.2 * mm});
            skCircle(sketch, "E297", {"center": v(3338.2, -177.16) * mm, "radius": 5.2 * mm});
            skLineSegment(sketch, "E298", {"start": v(3376.3, 32.2) * mm, "end": v(3376.3, -82.1) * mm});
            skCircle(sketch, "E299", {"center": v(4151, -24.76) * mm, "radius": 5.2 * mm});
            skCircle(sketch, "E300", {"center": v(4151, 26.04) * mm, "radius": 5.2 * mm});
            skCircle(sketch, "E301", {"center": v(4151, 127.64) * mm, "radius": 5.2 * mm});
            skCircle(sketch, "E302", {"center": v(4151, 76.84) * mm, "radius": 5.2 * mm});
            skLineSegment(sketch, "E303", {"start": v(4189.1, 32.2) * mm, "end": v(4189.1, -82.1) * mm});
            skArc(sketch, "E304", {"start": v(4189.1, 32.2) * mm, "mid": v(4185.39, 41.17) * mm, "end": v(4176.4, 44.9) * mm});
            skArc(sketch, "E305", {"start": v(4112.9, -82.1) * mm, "mid": v(4116.63, -91.09) * mm, "end": v(4125.6, -94.8) * mm});
            skLineSegment(sketch, "E306", {"start": v(4125.6, 44.9) * mm, "end": v(4176.4, 44.9) * mm});
            skArc(sketch, "E307", {"start": v(4125.6, 44.9) * mm, "mid": v(4116.63, 41.17) * mm, "end": v(4112.9, 32.2) * mm});
            skLineSegment(sketch, "E308", {"start": v(4125.6, -94.8) * mm, "end": v(4176.4, -94.8) * mm});
            skArc(sketch, "E309", {"start": v(4176.4, -94.8) * mm, "mid": v(4185.39, -91.09) * mm, "end": v(4189.1, -82.1) * mm});
            skCircle(sketch, "E310", {"center": v(4151, -24.96) * mm, "radius": 9.65 * mm});
            skCircle(sketch, "E311", {"center": v(4151, -126.36) * mm, "radius": 5.2 * mm});
            skCircle(sketch, "E312", {"center": v(4151, -75.56) * mm, "radius": 5.2 * mm});
            skCircle(sketch, "E313", {"center": v(4151, -177.16) * mm, "radius": 5.2 * mm});
            skLineSegment(sketch, "E314", {"start": v(4112.9, 32.2) * mm, "end": v(4112.9, -82.1) * mm});
            skLineSegment(sketch, "E315", {"start": v(-36.67, 1235.06) * mm, "end": v(1309.53, 1234.8) * mm});
            skLineSegment(sketch, "E316", {"start": v(-36.67, 1263.5) * mm, "end": v(1309.53, 1263.26) * mm});
            skLineSegment(sketch, "E317", {"start": v(-30.32, 1282.3) * mm, "end": v(-30.32, 1422) * mm});
            skLineSegment(sketch, "E318", {"start": v(4.34, 1301.36) * mm, "end": v(-30.32, 1301.36) * mm});
            skLineSegment(sketch, "E319", {"start": v(4.34, 1402.96) * mm, "end": v(-30.32, 1402.96) * mm});
            skLineSegment(sketch, "E320", {"start": v(-30.32, 1282.3) * mm, "end": v(-36.67, 1282.3) * mm});
            skLineSegment(sketch, "E321", {"start": v(-30.32, 1422) * mm, "end": v(-36.67, 1422) * mm});
            skLineSegment(sketch, "E322", {"start": v(-30.32, 1342.5) * mm, "end": v(166.53, 1342.5) * mm});
            skLineSegment(sketch, "E323", {"start": v(-30.32, 1361.8) * mm, "end": v(166.53, 1361.8) * mm});
            skLineSegment(sketch, "E324", {"start": v(166.53, 1361.8) * mm, "end": v(166.53, 1342.5) * mm});
            skLineSegment(sketch, "E325", {"start": v(1303.18, 1282.3) * mm, "end": v(1303.18, 1422) * mm});
            skLineSegment(sketch, "E326", {"start": v(1268.5, 1301.36) * mm, "end": v(1303.18, 1301.36) * mm});
            skLineSegment(sketch, "E327", {"start": v(1268.5, 1402.96) * mm, "end": v(1303.18, 1402.96) * mm});
            skLineSegment(sketch, "E328", {"start": v(1303.18, 1282.3) * mm, "end": v(1309.53, 1282.3) * mm});
            skLineSegment(sketch, "E329", {"start": v(1303.18, 1422) * mm, "end": v(1309.53, 1422) * mm});
            skLineSegment(sketch, "E330", {"start": v(1303.18, 1342.5) * mm, "end": v(1106.33, 1342.5) * mm});
            skLineSegment(sketch, "E331", {"start": v(1303.18, 1361.8) * mm, "end": v(1106.33, 1361.8) * mm});
            skLineSegment(sketch, "E332", {"start": v(1106.33, 1361.8) * mm, "end": v(1106.33, 1342.5) * mm});
            skLineSegment(sketch, "E333", {"start": v(1309.53, 1422) * mm, "end": v(1309.53, 1282.3) * mm});
            skLineSegment(sketch, "E334", {"start": v(-36.67, 1422) * mm, "end": v(-36.67, 1282.3) * mm});
            skLineSegment(sketch, "E335", {"start": v(236.38, 2109.63) * mm, "end": v(299.88, 2109.63) * mm});
            skLineSegment(sketch, "E336", {"start": v(258.47, 2046.13) * mm, "end": v(277.78, 2046.13) * mm});
            skLineSegment(sketch, "E337", {"start": v(268.13, 2074.97) * mm, "end": v(268.13, 2109.63) * mm});
            skLineSegment(sketch, "E338", {"start": v(236.38, 2109.63) * mm, "end": v(236.38, 2115.98) * mm});
            skLineSegment(sketch, "E339", {"start": v(299.88, 2109.63) * mm, "end": v(299.88, 2115.98) * mm});
            skLineSegment(sketch, "E340", {"start": v(258.47, 2109.63) * mm, "end": v(258.47, 2046.13) * mm});
            skLineSegment(sketch, "E341", {"start": v(277.78, 2109.63) * mm, "end": v(277.78, 2046.13) * mm});
            skLineSegment(sketch, "E342", {"start": v(299.88, 2115.98) * mm, "end": v(236.38, 2115.98) * mm});
            skLineSegment(sketch, "E343", {"start": v(1036.48, 2109.63) * mm, "end": v(972.98, 2109.63) * mm});
            skLineSegment(sketch, "E344", {"start": v(1014.38, 2046.13) * mm, "end": v(995.07, 2046.13) * mm});
            skLineSegment(sketch, "E345", {"start": v(1004.73, 2074.97) * mm, "end": v(1004.73, 2109.63) * mm});
            skLineSegment(sketch, "E346", {"start": v(1036.48, 2109.63) * mm, "end": v(1036.48, 2115.98) * mm});
            skLineSegment(sketch, "E347", {"start": v(972.98, 2109.63) * mm, "end": v(972.98, 2115.98) * mm});
            skLineSegment(sketch, "E348", {"start": v(1014.38, 2109.63) * mm, "end": v(1014.38, 2046.13) * mm});
            skLineSegment(sketch, "E349", {"start": v(995.07, 2109.63) * mm, "end": v(995.07, 2046.13) * mm});
            skLineSegment(sketch, "E350", {"start": v(972.98, 2115.98) * mm, "end": v(1036.48, 2115.98) * mm});
            skLineSegment(sketch, "E351", {"start": v(-127.94, 2253.51) * mm, "end": v(-127.94, 2043.96) * mm});
            skLineSegment(sketch, "E352", {"start": v(-262.56, 2253.51) * mm, "end": v(-262.56, 2043.96) * mm});
            skLineSegment(sketch, "E353", {"start": v(-249.86, 2253.51) * mm, "end": v(-249.86, 2043.96) * mm});
            skLineSegment(sketch, "E354", {"start": v(-124, 2043.96) * mm, "end": v(-262.56, 2043.96) * mm});
            skLineSegment(sketch, "E355", {"start": v(-124, 2253.51) * mm, "end": v(-262.56, 2253.51) * mm});
            skLineSegment(sketch, "E356", {"start": v(-3895.3, -1662.57) * mm, "end": v(-2706.12, -1662.57) * mm});
            skArc(sketch, "E357", {"start": v(-2676.1, -1662.57) * mm, "mid": v(-1841.27, 748.35) * mm, "end": v(-3752.6, 2438.4) * mm});
            skLineSegment(sketch, "E358", {"start": v(-3936.53, 538.91) * mm, "end": v(-4798.63, 1401.02) * mm});
            skLineSegment(sketch, "E359", {"start": v(-4798.63, 1401.02) * mm, "end": v(-3756.92, 2442.73) * mm});
            skLineSegment(sketch, "E360", {"start": v(-3756.92, 2442.73) * mm, "end": v(-2894.82, 1580.62) * mm});
            skLineSegment(sketch, "E361", {"start": v(-2894.82, 1580.62) * mm, "end": v(-3936.53, 538.91) * mm});
            skCircle(sketch, "E362", {"center": v(3338.2, -227.96) * mm, "radius": 5.2 * mm});
            skCircle(sketch, "E363", {"center": v(3338.2, -278.76) * mm, "radius": 5.2 * mm});
            skCircle(sketch, "E364", {"center": v(4151, -227.96) * mm, "radius": 5.2 * mm});
            skCircle(sketch, "E365", {"center": v(4151, -278.76) * mm, "radius": 5.2 * mm});
            skCircle(sketch, "E366", {"center": v(3338.2, -329.56) * mm, "radius": 5.2 * mm});
            skCircle(sketch, "E367", {"center": v(3338.2, -380.36) * mm, "radius": 5.2 * mm});
            skCircle(sketch, "E368", {"center": v(4151, -329.56) * mm, "radius": 5.2 * mm});
            skCircle(sketch, "E369", {"center": v(4151, -380.36) * mm, "radius": 5.2 * mm});
            skCircle(sketch, "E370", {"center": v(-3126.94, -290.97) * mm, "radius": 7.5 * mm});
            skCircle(sketch, "E371", {"center": v(-3126.94, -443.37) * mm, "radius": 7.5 * mm});
            skCircle(sketch, "E372", {"center": v(-3126.94, -392.57) * mm, "radius": 7.5 * mm});
            skCircle(sketch, "E373", {"center": v(-3126.94, -341.77) * mm, "radius": 7.5 * mm});
            skLineSegment(sketch, "E374", {"start": v(-1561.44, -1652.71) * mm, "end": v(-1561.44, 176.09) * mm});
            skLineSegment(sketch, "E375", {"start": v(-1478.63, -1656.22) * mm, "end": v(-1478.63, 832.98) * mm});
            skLineSegment(sketch, "E376", {"start": v(-1481.94, -1656.22) * mm, "end": v(-1478.63, -1656.22) * mm});
            skLineSegment(sketch, "E377", {"start": v(-1561.44, -1656.22) * mm, "end": v(-1561.44, 832.98) * mm});
            skLineSegment(sketch, "E378", {"start": v(-1558.03, -1656.22) * mm, "end": v(-1558.03, 832.98) * mm});
            skLineSegment(sketch, "E379", {"start": v(-1456.54, -1662.57) * mm, "end": v(-1621.89, -1662.57) * mm});
            skLineSegment(sketch, "E380", {"start": v(-1621.89, -1662.57) * mm, "end": v(-1621.89, -1656.22) * mm});
            skLineSegment(sketch, "E381", {"start": v(-1621.89, -1656.22) * mm, "end": v(-1456.54, -1656.22) * mm});
            skLineSegment(sketch, "E382", {"start": v(-1561.44, 832.98) * mm, "end": v(-1478.63, 832.98) * mm});
            skLineSegment(sketch, "E383", {"start": v(-1482.04, -1656.22) * mm, "end": v(-1482.04, 832.98) * mm});
            skLineSegment(sketch, "E384", {"start": v(-1478.63, 623.18) * mm, "end": v(-1440.53, 623.18) * mm});
            skLineSegment(sketch, "E385", {"start": v(-1440.53, 626.58) * mm, "end": v(-1475.23, 626.58) * mm});
            skLineSegment(sketch, "E386", {"start": v(-1475.23, 626.58) * mm, "end": v(-1475.23, 829.58) * mm});
            skLineSegment(sketch, "E387", {"start": v(-1478.63, 832.98) * mm, "end": v(-1440.53, 832.98) * mm});
            skLineSegment(sketch, "E388", {"start": v(-1440.53, 829.58) * mm, "end": v(-1475.23, 829.58) * mm});
            skLineSegment(sketch, "E389", {"start": v(-1440.53, 832.98) * mm, "end": v(-1440.53, 829.58) * mm});
            skLineSegment(sketch, "E390", {"start": v(-1440.53, 626.58) * mm, "end": v(-1440.53, 623.18) * mm});
            skLineSegment(sketch, "E391", {"start": v(-3415.64, 737.73) * mm, "end": v(-1612.24, 737.73) * mm});
            skLineSegment(sketch, "E392", {"start": v(-1612.24, -1599.07) * mm, "end": v(-3415.64, -1599.07) * mm});
            skLineSegment(sketch, "E393", {"start": v(-1561.44, -1649.87) * mm, "end": v(-3466.44, -1649.87) * mm});
            skLineSegment(sketch, "E394", {"start": v(-3466.44, 788.53) * mm, "end": v(-1561.44, 788.53) * mm});
            skLineSegment(sketch, "E395", {"start": v(-3415.64, -1599.07) * mm, "end": v(-3415.64, 737.73) * mm});
            skLineSegment(sketch, "E396", {"start": v(-3466.44, -1649.87) * mm, "end": v(-3466.44, 788.53) * mm});
            skLineSegment(sketch, "E397", {"start": v(-1612.24, -1599.07) * mm, "end": v(-1612.24, 737.73) * mm});
            skLineSegment(sketch, "E398", {"start": v(-1561.44, -1649.87) * mm, "end": v(-1561.44, 788.53) * mm});
            skLineSegment(sketch, "E399", {"start": v(-3415.64, -1014.87) * mm, "end": v(-1612.24, -1014.87) * mm});
            skLineSegment(sketch, "E400", {"start": v(-3415.64, -1065.67) * mm, "end": v(-1612.24, -1065.67) * mm});
            skLineSegment(sketch, "E401", {"start": v(-3409.96, -1014.87) * mm, "end": v(-3415.64, -1005.03) * mm});
            skLineSegment(sketch, "E402", {"start": v(-2148.77, -1014.87) * mm, "end": v(-2147.62, -1012.88) * mm});
            skLineSegment(sketch, "E403", {"start": v(-3415.64, 204.33) * mm, "end": v(-1612.24, 204.33) * mm});
            skLineSegment(sketch, "E404", {"start": v(-3415.64, 153.53) * mm, "end": v(-1612.24, 153.53) * mm});
            skLineSegment(sketch, "E405", {"start": v(-1612.98, 204.33) * mm, "end": v(-1612.24, 205.62) * mm});
            skLineSegment(sketch, "E406", {"start": v(-3409.96, 204.33) * mm, "end": v(-3415.64, 214.17) * mm});
            skLineSegment(sketch, "E407", {"start": v(-3415.64, 737.73) * mm, "end": v(-3466.44, 788.53) * mm});
            skLineSegment(sketch, "E408", {"start": v(-1612.24, 737.73) * mm, "end": v(-1561.44, 788.53) * mm});
            skLineSegment(sketch, "E409", {"start": v(-1561.44, -1649.87) * mm, "end": v(-1612.24, -1599.07) * mm});
            skLineSegment(sketch, "E410", {"start": v(-3466.44, -1649.87) * mm, "end": v(-3415.64, -1599.07) * mm});
            skLineSegment(sketch, "E411", {"start": v(-3415.64, -405.27) * mm, "end": v(-1612.24, -405.27) * mm});
            skLineSegment(sketch, "E412", {"start": v(-3415.64, -456.07) * mm, "end": v(-1612.24, -456.07) * mm});
            skLineSegment(sketch, "E413", {"start": v(-3984.25, 240.85) * mm, "end": v(-3984.25, 97.97) * mm});
            skLineSegment(sketch, "E414", {"start": v(-3466.44, 788.53) * mm, "end": v(-4168.34, 788.53) * mm});
            skLineSegment(sketch, "E415", {"start": v(-3415.64, 344.03) * mm, "end": v(-3308.19, 344.03) * mm});
            skArc(sketch, "E416", {"start": v(-3990.6, 91.62) * mm, "mid": v(-3986.11, 93.48) * mm, "end": v(-3984.25, 97.97) * mm});
            skLineSegment(sketch, "E417", {"start": v(-4133.48, 91.62) * mm, "end": v(-3990.6, 91.62) * mm});
            skLineSegment(sketch, "E418", {"start": v(-4168.34, 240.85) * mm, "end": v(-4168.34, 788.53) * mm});
            skLineSegment(sketch, "E419", {"start": v(-4133.48, 240.85) * mm, "end": v(-3984.25, 240.85) * mm});
            skLineSegment(sketch, "E420", {"start": v(-4168.34, 788.53) * mm, "end": v(-4168.34, -278.27) * mm});
            skLineSegment(sketch, "E421", {"start": v(-4168.34, -278.27) * mm, "end": v(-4193.74, -278.27) * mm});
            skLineSegment(sketch, "E422", {"start": v(-4193.74, -278.27) * mm, "end": v(-4193.74, 788.53) * mm});
            skLineSegment(sketch, "E423", {"start": v(-4193.74, 788.53) * mm, "end": v(-4168.34, 788.53) * mm});
            skLineSegment(sketch, "E424", {"start": v(-4133.48, 91.62) * mm, "end": v(-4133.48, 240.85) * mm});
            skLineSegment(sketch, "E425", {"start": v(-4193.74, -278.27) * mm, "end": v(-4193.74, -1662.57) * mm});
            skLineSegment(sketch, "E426", {"start": v(-4193.74, -1662.57) * mm, "end": v(-4117.54, -1662.57) * mm});
            skLineSegment(sketch, "E427", {"start": v(-123.35, 2414.43) * mm, "end": v(-123.35, 2335.19) * mm});
            skLineSegment(sketch, "E428", {"start": v(1395.58, 2414.43) * mm, "end": v(1395.58, 2325.63) * mm});
            skLineSegment(sketch, "E429", {"start": v(-72.55, 2414.43) * mm, "end": v(1344.78, 2414.43) * mm});
            skLineSegment(sketch, "E430", {"start": v(1344.78, 2414.43) * mm, "end": v(1344.78, 2389.03) * mm});
            skLineSegment(sketch, "E431", {"start": v(1344.78, 2389.03) * mm, "end": v(-72.55, 2389.03) * mm});
            skLineSegment(sketch, "E432", {"start": v(-72.55, 2389.03) * mm, "end": v(-72.55, 2414.43) * mm});
            skLineSegment(sketch, "E433", {"start": v(-4193.74, -290.97) * mm, "end": v(-4168.34, -290.97) * mm});
            skLineSegment(sketch, "E434", {"start": v(-4168.34, -290.97) * mm, "end": v(-4168.34, -1662.57) * mm});
            skLineSegment(sketch, "E435", {"start": v(-4168.34, -1662.57) * mm, "end": v(-4193.74, -1662.57) * mm});
            skLineSegment(sketch, "E436", {"start": v(-4193.74, -1662.57) * mm, "end": v(-4193.74, -290.97) * mm});
            skLineSegment(sketch, "E437", {"start": v(1306.68, 2419) * mm, "end": v(1382.9, 2419) * mm});
            skLineSegment(sketch, "E438", {"start": v(1382.9, 2419) * mm, "end": v(1382.9, 2414.43) * mm});
            skLineSegment(sketch, "E439", {"start": v(1382.9, 2414.43) * mm, "end": v(1306.68, 2414.43) * mm});
            skLineSegment(sketch, "E440", {"start": v(1306.68, 2414.43) * mm, "end": v(1306.68, 2419) * mm});
            skLineSegment(sketch, "E441", {"start": v(1395.58, 2414.43) * mm, "end": v(1357.48, 2414.43) * mm});
            skLineSegment(sketch, "E442", {"start": v(1357.48, 2414.43) * mm, "end": v(1357.48, 2409.86) * mm});
            skLineSegment(sketch, "E443", {"start": v(1357.48, 2409.86) * mm, "end": v(1391.01, 2409.86) * mm});
            skLineSegment(sketch, "E444", {"start": v(1391.01, 2409.86) * mm, "end": v(1391.01, 2338.23) * mm});
            skLineSegment(sketch, "E445", {"start": v(-85.25, 2414.43) * mm, "end": v(-85.25, 2409.86) * mm});
            skLineSegment(sketch, "E446", {"start": v(-85.25, 2409.86) * mm, "end": v(-118.77, 2409.86) * mm});
            skLineSegment(sketch, "E447", {"start": v(-118.77, 2409.86) * mm, "end": v(-118.77, 2338.23) * mm});
            skLineSegment(sketch, "E448", {"start": v(-34.45, 2419) * mm, "end": v(-110.67, 2419) * mm});
            skLineSegment(sketch, "E449", {"start": v(-110.67, 2419) * mm, "end": v(-110.67, 2414.43) * mm});
            skLineSegment(sketch, "E450", {"start": v(-110.67, 2414.43) * mm, "end": v(-34.45, 2414.43) * mm});
            skLineSegment(sketch, "E451", {"start": v(-34.45, 2414.43) * mm, "end": v(-34.45, 2419) * mm});
            skLineSegment(sketch, "E452", {"start": v(-85.25, 2414.43) * mm, "end": v(-123.35, 2414.43) * mm});
            skLineSegment(sketch, "E453", {"start": v(2879.74, 633.12) * mm, "end": v(4607.95, 633.12) * mm});
            skLineSegment(sketch, "E454", {"start": v(2879.74, 636.42) * mm, "end": v(4607.95, 636.42) * mm});
            skLineSegment(sketch, "E455", {"start": v(2879.74, 833.27) * mm, "end": v(4607.95, 833.27) * mm});
            skLineSegment(sketch, "E456", {"start": v(2851.04, 836.57) * mm, "end": v(4636.66, 836.57) * mm});
            skLineSegment(sketch, "E457", {"start": v(4560.46, -1652.63) * mm, "end": v(4560.46, 633.12) * mm});
            skLineSegment(sketch, "E458", {"start": v(4636.66, -1652.63) * mm, "end": v(4636.66, 836.57) * mm});
            skLineSegment(sketch, "E459", {"start": v(4633.25, -1652.63) * mm, "end": v(4633.25, 836.57) * mm});
            skLineSegment(sketch, "E460", {"start": v(4538.36, -1652.63) * mm, "end": v(4538.36, -1658.98) * mm});
            skLineSegment(sketch, "E461", {"start": v(4697.1, -1658.98) * mm, "end": v(4697.1, -1652.63) * mm});
            skLineSegment(sketch, "E462", {"start": v(4697.1, -1652.63) * mm, "end": v(4538.36, -1652.63) * mm});
            skLineSegment(sketch, "E463", {"start": v(2879.74, 836.57) * mm, "end": v(2879.74, 633.12) * mm});
            skLineSegment(sketch, "E464", {"start": v(4607.95, 836.57) * mm, "end": v(4607.95, 633.12) * mm});
            skLineSegment(sketch, "E465", {"start": v(2927.24, -1652.63) * mm, "end": v(2927.24, 633.12) * mm});
            skLineSegment(sketch, "E466", {"start": v(2851.04, -1652.63) * mm, "end": v(2851.04, 836.57) * mm});
            skLineSegment(sketch, "E467", {"start": v(2854.44, -1652.63) * mm, "end": v(2854.44, 836.57) * mm});
            skLineSegment(sketch, "E468", {"start": v(2949.33, -1652.63) * mm, "end": v(2949.33, -1658.98) * mm});
            skLineSegment(sketch, "E469", {"start": v(4697.1, -1658.98) * mm, "end": v(2790.58, -1658.98) * mm});
            skLineSegment(sketch, "E470", {"start": v(2790.58, -1658.98) * mm, "end": v(2790.58, -1652.63) * mm});
            skLineSegment(sketch, "E471", {"start": v(2790.58, -1652.63) * mm, "end": v(2949.33, -1652.63) * mm});
            skCircle(sketch, "E472", {"center": v(4588.9, 814.22) * mm, "radius": 5.08 * mm});
            skCircle(sketch, "E473", {"center": v(4588.9, 661.82) * mm, "radius": 5.08 * mm});
            skCircle(sketch, "E474", {"center": v(2898.79, 814.22) * mm, "radius": 5.08 * mm});
            skCircle(sketch, "E475", {"center": v(2898.79, 661.82) * mm, "radius": 5.08 * mm});
            skLineSegment(sketch, "E476", {"start": v(-809.15, 2401.73) * mm, "end": v(-123.35, 2401.73) * mm});
            skLineSegment(sketch, "E477", {"start": v(-123.35, 2401.73) * mm, "end": v(-123.35, 2376.33) * mm});
            skLineSegment(sketch, "E478", {"start": v(-123.35, 2376.33) * mm, "end": v(-809.15, 2376.33) * mm});
            skLineSegment(sketch, "E479", {"start": v(-809.15, 2376.33) * mm, "end": v(-809.15, 2401.73) * mm});
            skLineSegment(sketch, "E480", {"start": v(2081.38, 2401.73) * mm, "end": v(1395.58, 2401.73) * mm});
            skLineSegment(sketch, "E481", {"start": v(1395.58, 2401.73) * mm, "end": v(1395.58, 2376.33) * mm});
            skLineSegment(sketch, "E482", {"start": v(1395.58, 2376.33) * mm, "end": v(2081.38, 2376.33) * mm});
            skLineSegment(sketch, "E483", {"start": v(2081.38, 2376.33) * mm, "end": v(2081.38, 2401.73) * mm});
            skLineSegment(sketch, "E484", {"start": v(2851.04, -274.68) * mm, "end": v(2299.37, -274.68) * mm});
            skLineSegment(sketch, "E485", {"start": v(2299.37, -274.68) * mm, "end": v(2299.37, 792.12) * mm});
            skLineSegment(sketch, "E486", {"start": v(2299.37, 792.12) * mm, "end": v(2851.04, 792.12) * mm});
            skLineSegment(sketch, "E487", {"start": v(2851.04, -223.88) * mm, "end": v(2350.17, -223.88) * mm});
            skLineSegment(sketch, "E488", {"start": v(2350.17, -223.88) * mm, "end": v(2350.17, 741.32) * mm});
            skLineSegment(sketch, "E489", {"start": v(2350.17, 741.32) * mm, "end": v(2851.04, 741.32) * mm});
            skLineSegment(sketch, "E490", {"start": v(4636.66, 792.12) * mm, "end": v(5194.97, 792.12) * mm});
            skLineSegment(sketch, "E491", {"start": v(5194.97, 792.12) * mm, "end": v(5194.97, -274.68) * mm});
            skLineSegment(sketch, "E492", {"start": v(5194.97, -274.68) * mm, "end": v(4636.66, -274.68) * mm});
            skLineSegment(sketch, "E493", {"start": v(4636.66, 741.32) * mm, "end": v(5144.17, 741.32) * mm});
            skLineSegment(sketch, "E494", {"start": v(5144.17, 741.32) * mm, "end": v(5144.17, -223.88) * mm});
            skLineSegment(sketch, "E495", {"start": v(5144.17, -223.88) * mm, "end": v(4636.66, -223.88) * mm});
            skLineSegment(sketch, "E496", {"start": v(2299.37, -274.68) * mm, "end": v(2350.17, -223.88) * mm});
            skLineSegment(sketch, "E497", {"start": v(5144.17, -223.88) * mm, "end": v(5194.97, -274.68) * mm});
            skLineSegment(sketch, "E498", {"start": v(5194.97, 792.12) * mm, "end": v(5144.17, 741.32) * mm});
            skLineSegment(sketch, "E499", {"start": v(-3638.87, -416.28) * mm, "end": v(-3880.43, -416.28) * mm});
            skArc(sketch, "E500", {"start": v(-3889.82, -391.13) * mm, "mid": v(-3887.07, -397.78) * mm, "end": v(-3880.43, -400.53) * mm});
            skLineSegment(sketch, "E501", {"start": v(-3638.87, -400.53) * mm, "end": v(-3880.43, -400.53) * mm});
            skLineSegment(sketch, "E502", {"start": v(-3629.47, -406.88) * mm, "end": v(-3629.47, -133.83) * mm});
            skLineSegment(sketch, "E503", {"start": v(-3889.82, -406.88) * mm, "end": v(-3889.82, -133.83) * mm});
            skArc(sketch, "E504", {"start": v(-3638.87, -400.53) * mm, "mid": v(-3632.23, -397.78) * mm, "end": v(-3629.47, -391.13) * mm});
            skArc(sketch, "E505", {"start": v(-3638.87, -416.28) * mm, "mid": v(-3632.23, -413.52) * mm, "end": v(-3629.47, -406.88) * mm});
            skArc(sketch, "E506", {"start": v(-3889.82, -406.88) * mm, "mid": v(-3887.07, -413.52) * mm, "end": v(-3880.43, -416.28) * mm});
            skLineSegment(sketch, "E507", {"start": v(-3880.43, -124.43) * mm, "end": v(-3638.87, -124.43) * mm});
            skLineSegment(sketch, "E508", {"start": v(-3880.43, -140.18) * mm, "end": v(-3638.87, -140.18) * mm});
            skCircle(sketch, "E509", {"center": v(-3841.08, -186.95) * mm, "radius": 12.7 * mm});
            skLineSegment(sketch, "E510", {"start": v(-3811.87, -239.58) * mm, "end": v(-3867.88, -239.58) * mm});
            skLineSegment(sketch, "E511", {"start": v(-3867.88, -214.81) * mm, "end": v(-3811.87, -214.81) * mm});
            skLineSegment(sketch, "E512", {"start": v(-3867.88, -239.58) * mm, "end": v(-3867.88, -214.81) * mm});
            skLineSegment(sketch, "E513", {"start": v(-3811.87, -214.81) * mm, "end": v(-3811.87, -239.58) * mm});
            skCircle(sketch, "E514", {"center": v(-3841.08, -186.95) * mm, "radius": 15.75 * mm});
            skArc(sketch, "E515", {"start": v(-3880.43, -124.43) * mm, "mid": v(-3887.07, -127.18) * mm, "end": v(-3889.82, -133.83) * mm});
            skArc(sketch, "E516", {"start": v(-3880.43, -140.18) * mm, "mid": v(-3887.07, -142.93) * mm, "end": v(-3889.82, -149.58) * mm});
            skCircle(sketch, "E517", {"center": v(-3739.27, -186.95) * mm, "radius": 12.7 * mm});
            skLineSegment(sketch, "E518", {"start": v(-3766.47, -214.81) * mm, "end": v(-3710.46, -214.81) * mm});
            skCircle(sketch, "E519", {"center": v(-3739.27, -186.95) * mm, "radius": 15.75 * mm});
            skLineSegment(sketch, "E520", {"start": v(-3710.46, -239.58) * mm, "end": v(-3766.47, -239.58) * mm});
            skLineSegment(sketch, "E521", {"start": v(-3766.47, -239.58) * mm, "end": v(-3766.47, -214.81) * mm});
            skLineSegment(sketch, "E522", {"start": v(-3710.46, -214.81) * mm, "end": v(-3710.46, -239.58) * mm});
            skArc(sketch, "E523", {"start": v(-3629.47, -133.83) * mm, "mid": v(-3632.23, -127.18) * mm, "end": v(-3638.87, -124.43) * mm});
            skArc(sketch, "E524", {"start": v(-3629.47, -149.58) * mm, "mid": v(-3632.23, -142.93) * mm, "end": v(-3638.87, -140.18) * mm});
            skArc(sketch, "E525", {"start": v(-3838.4, -324.84) * mm, "mid": v(-3828.64, -320.34) * mm, "end": v(-3824.66, -310.37) * mm});
            skArc(sketch, "E526", {"start": v(-3840.07, -292.47) * mm, "mid": v(-3852.15, -298.02) * mm, "end": v(-3857.08, -310.37) * mm});
            skCircle(sketch, "E527", {"center": v(-3839.16, -310.37) * mm, "radius": 19.94 * mm});
            skLineSegment(sketch, "E528", {"start": v(-3857.08, -310.37) * mm, "end": v(-3855.36, -308.66) * mm});
            skLineSegment(sketch, "E529", {"start": v(-3855.36, -308.66) * mm, "end": v(-3853.65, -310.37) * mm});
            skLineSegment(sketch, "E530", {"start": v(-3840.07, -292.47) * mm, "end": v(-3838.32, -294.55) * mm});
            skLineSegment(sketch, "E531", {"start": v(-3838.32, -294.55) * mm, "end": v(-3839.92, -295.9) * mm});
            skLineSegment(sketch, "E532", {"start": v(-3838.4, -324.84) * mm, "end": v(-3839.99, -326.19) * mm});
            skLineSegment(sketch, "E533", {"start": v(-3839.99, -326.19) * mm, "end": v(-3838.24, -328.27) * mm});
            skLineSegment(sketch, "E534", {"start": v(-3824.66, -310.37) * mm, "end": v(-3822.95, -312.08) * mm});
            skLineSegment(sketch, "E535", {"start": v(-3822.95, -312.08) * mm, "end": v(-3821.23, -310.36) * mm});
            skArc(sketch, "E536", {"start": v(-3839.92, -295.9) * mm, "mid": v(-3849.67, -300.4) * mm, "end": v(-3853.65, -310.37) * mm});
            skArc(sketch, "E537", {"start": v(-3838.24, -328.27) * mm, "mid": v(-3826.16, -322.71) * mm, "end": v(-3821.23, -310.36) * mm});
            skCircle(sketch, "E538", {"center": v(-3839.16, -310.37) * mm, "radius": 30 * mm});
            skLineSegment(sketch, "E539", {"start": v(-4274.7, 104.05) * mm, "end": v(-4220.82, 157.93) * mm});
            skLineSegment(sketch, "E540", {"start": v(-4116.02, 46.3) * mm, "end": v(-4224.23, 154.52) * mm});
            skLineSegment(sketch, "E541", {"start": v(-4116.02, -68.9) * mm, "end": v(-4116.02, 58.35) * mm});
            skLineSegment(sketch, "E542", {"start": v(-4116.02, 58.35) * mm, "end": v(-4109.67, 58.35) * mm});
            skLineSegment(sketch, "E543", {"start": v(-4116.02, 53.13) * mm, "end": v(-4246.14, 183.25) * mm});
            skLineSegment(sketch, "E544", {"start": v(-4116.02, 46.3) * mm, "end": v(-4249.56, 179.84) * mm});
            skLineSegment(sketch, "E545", {"start": v(-4116.02, -54.64) * mm, "end": v(-4300.03, 129.37) * mm});
            skLineSegment(sketch, "E546", {"start": v(-4116.02, -47.81) * mm, "end": v(-4296.61, 132.79) * mm});
            skLineSegment(sketch, "E547", {"start": v(-4287.58, 135.71) * mm, "end": v(-4252.49, 170.8) * mm});
            skLineSegment(sketch, "E548", {"start": v(-4271.33, 107.42) * mm, "end": v(-4288.08, 129.57) * mm});
            skLineSegment(sketch, "E549", {"start": v(-4224.19, 154.56) * mm, "end": v(-4246.35, 171.31) * mm});
            skArc(sketch, "E550", {"start": v(-4290.95, 139.08) * mm, "mid": v(-4293.7, 133.13) * mm, "end": v(-4291.96, 126.8) * mm});
            skArc(sketch, "E551", {"start": v(-4243.57, 175.19) * mm, "mid": v(-4249.9, 176.93) * mm, "end": v(-4255.85, 174.18) * mm});
            skLineSegment(sketch, "E552", {"start": v(-4300.03, 129.37) * mm, "end": v(-4246.14, 183.25) * mm});
            skLineSegment(sketch, "E553", {"start": v(-4109.67, 58.35) * mm, "end": v(-4109.67, -68.9) * mm});
            skLineSegment(sketch, "E554", {"start": v(-4116.02, -68.9) * mm, "end": v(-4109.67, -68.9) * mm});
            skLineSegment(sketch, "E555", {"start": v(-3464.91, 2158.6) * mm, "end": v(-2890.18, 1583.86) * mm});
            skLineSegment(sketch, "E556", {"start": v(-2890.18, 1583.86) * mm, "end": v(-3674.62, 568.44) * mm});
            skLineSegment(sketch, "E557", {"start": v(-4219.25, 254.78) * mm, "end": v(-4058.87, 94.4) * mm});
            skLineSegment(sketch, "E558", {"start": v(-4058.87, 94.4) * mm, "end": v(-3986.98, 166.28) * mm});
            skLineSegment(sketch, "E559", {"start": v(-4309.06, 164.98) * mm, "end": v(-2890.18, 1583.86) * mm});
            skLineSegment(sketch, "E560", {"start": v(-3641.28, 2341.43) * mm, "end": v(-2886.94, 1587.09) * mm});
            skLineSegment(sketch, "E561", {"start": v(-4305.82, 161.74) * mm, "end": v(-4216.02, 251.55) * mm});
            skLineSegment(sketch, "E562", {"start": v(-3464.91, 2158.6) * mm, "end": v(-3644.52, 2338.2) * mm});
            skLineSegment(sketch, "E563", {"start": v(-3641.28, 2341.43) * mm, "end": v(-3644.52, 2338.2) * mm});
            skLineSegment(sketch, "E564", {"start": v(-4309.06, 164.98) * mm, "end": v(-4722.15, 578.07) * mm});
            skLineSegment(sketch, "E565", {"start": v(-3999.44, 468.12) * mm, "end": v(-4071.28, 396.28) * mm});
            skLineSegment(sketch, "E566", {"start": v(-3970.35, 439.03) * mm, "end": v(-4042.19, 367.19) * mm});
            skLineSegment(sketch, "E567", {"start": v(-4042.19, 367.19) * mm, "end": v(-4071.28, 396.28) * mm});
            skLineSegment(sketch, "E568", {"start": v(-3984.24, 432.31) * mm, "end": v(-4035.47, 381.08) * mm});
            skLineSegment(sketch, "E569", {"start": v(-4067.7, 399.87) * mm, "end": v(-4042.12, 380.62) * mm});
            skLineSegment(sketch, "E570", {"start": v(-4003.03, 464.53) * mm, "end": v(-3983.78, 438.96) * mm});
            skArc(sketch, "E571", {"start": v(-4035.47, 381.08) * mm, "mid": v(-4039.42, 389.74) * mm, "end": v(-4042.12, 380.62) * mm});
            skArc(sketch, "E572", {"start": v(-3983.78, 438.96) * mm, "mid": v(-3992.9, 436.26) * mm, "end": v(-3984.24, 432.31) * mm});
            skLineSegment(sketch, "E573", {"start": v(-4144.18, 323.39) * mm, "end": v(-3987.02, 166.23) * mm});
            skLineSegment(sketch, "E574", {"start": v(-4075.57, 254.78) * mm, "end": v(-3213.47, 1116.88) * mm});
            skLineSegment(sketch, "E575", {"start": v(-3213.47, 1116.88) * mm, "end": v(-3285.3, 1188.73) * mm});
            skLineSegment(sketch, "E576", {"start": v(-4305.82, 161.74) * mm, "end": v(-2886.94, 1580.62) * mm});
            skLineSegment(sketch, "E577", {"start": v(-3878.2, 580.38) * mm, "end": v(-3910.96, 522.03) * mm});
            skLineSegment(sketch, "E578", {"start": v(-3878.2, 580.38) * mm, "end": v(-3882.7, 584.87) * mm});
            skLineSegment(sketch, "E579", {"start": v(-3912.52, 456.2) * mm, "end": v(-3927.57, 441.15) * mm});
            skArc(sketch, "E580", {"start": v(-3972.47, 441.15) * mm, "mid": v(-3950.02, 431.86) * mm, "end": v(-3927.57, 441.15) * mm});
            skArc(sketch, "E581", {"start": v(-3912.52, 456.2) * mm, "mid": v(-3901.63, 478.63) * mm, "end": v(-3906.93, 502.98) * mm});
            skLineSegment(sketch, "E582", {"start": v(-3906.93, 502.98) * mm, "end": v(-3910.73, 509.2) * mm});
            skArc(sketch, "E583", {"start": v(-3910.96, 522.03) * mm, "mid": v(-3912.58, 515.59) * mm, "end": v(-3910.73, 509.2) * mm});
            skCircle(sketch, "E584", {"center": v(-3943.32, 479.35) * mm, "radius": 0.76 * mm});
            skCircle(sketch, "E585", {"center": v(-3924.28, 498.39) * mm, "radius": 0.5 * mm});
            skCircle(sketch, "E586", {"center": v(-3962.35, 460.31) * mm, "radius": 0.5 * mm});
            skLineSegment(sketch, "E587", {"start": v(-3999.44, 468.12) * mm, "end": v(-3882.7, 584.87) * mm});
            skLineSegment(sketch, "E588", {"start": v(-3972.47, 441.15) * mm, "end": v(-3999.44, 468.12) * mm});
            skLineSegment(sketch, "E589", {"start": v(-4694.58, 1058.94) * mm, "end": v(-4135.32, 229.8) * mm});
            skLineSegment(sketch, "E590", {"start": v(-4135.32, 229.8) * mm, "end": v(-4093.2, 258.2) * mm});
            skLineSegment(sketch, "E591", {"start": v(-4136.74, 231.9) * mm, "end": v(-4094.62, 260.31) * mm});
            skLineSegment(sketch, "E592", {"start": v(-4093.2, 258.2) * mm, "end": v(-4660.73, 1099.6) * mm});
            skLineSegment(sketch, "E593", {"start": v(-4691.3, 1062.25) * mm, "end": v(-4132.95, 234.46) * mm});
            skLineSegment(sketch, "E594", {"start": v(-4663.75, 1095.9) * mm, "end": v(-4098.41, 257.75) * mm});
            skArc(sketch, "E595", {"start": v(-3986.98, 184.24) * mm, "mid": v(-4008.66, 175.26) * mm, "end": v(-3986.98, 166.28) * mm});
            skLineSegment(sketch, "E596", {"start": v(-3986.98, 184.24) * mm, "end": v(-4004.94, 202.2) * mm});
            skLineSegment(sketch, "E597", {"start": v(-3986.98, 184.24) * mm, "end": v(-4013.92, 211.18) * mm});
            skArc(sketch, "E598", {"start": v(-4013.92, 211.18) * mm, "mid": v(-3992.24, 220.16) * mm, "end": v(-4013.92, 229.14) * mm});
            skLineSegment(sketch, "E599", {"start": v(-4013.92, 229.14) * mm, "end": v(-3674.62, 568.44) * mm});
            skLineSegment(sketch, "E600", {"start": v(-4220.51, 256.04) * mm, "end": v(-4058.87, 94.4) * mm});
            skLineSegment(sketch, "E601", {"start": v(-3645.77, 2339.46) * mm, "end": v(-4815.02, 911.12) * mm});
            skLineSegment(sketch, "E602", {"start": v(-2891.43, 1585.11) * mm, "end": v(-3669.69, 573.37) * mm});
            skLineSegment(sketch, "E603", {"start": v(-3645.77, 2339.46) * mm, "end": v(-2891.43, 1585.11) * mm});
            skCircle(sketch, "E604", {"center": v(-4058.87, 166.23) * mm, "radius": 25.9 * mm});
            skLineSegment(sketch, "E605", {"start": v(-3706.54, 2345.43) * mm, "end": v(-4806.06, 1002.26) * mm});
            skLineSegment(sketch, "E606", {"start": v(-4815.02, 911.12) * mm, "end": v(-4806.06, 1002.26) * mm});
            skLineSegment(sketch, "E607", {"start": v(-3645.77, 2339.46) * mm, "end": v(-3706.54, 2345.43) * mm});
            skCircle(sketch, "E608", {"center": v(-4597.68, 956.5) * mm, "radius": 6.86 * mm});
            skCircle(sketch, "E609", {"center": v(-4561.76, 992.42) * mm, "radius": 6.86 * mm});
            skCircle(sketch, "E610", {"center": v(-4525.84, 1028.34) * mm, "radius": 6.86 * mm});
            skCircle(sketch, "E611", {"center": v(-4489.92, 1064.26) * mm, "radius": 6.86 * mm});
            skCircle(sketch, "E612", {"center": v(-4454, 1100.18) * mm, "radius": 6.86 * mm});
            skCircle(sketch, "E613", {"center": v(-4346.23, 1207.94) * mm, "radius": 6.86 * mm});
            skCircle(sketch, "E614", {"center": v(-4382.16, 1172.02) * mm, "radius": 6.86 * mm});
            skCircle(sketch, "E615", {"center": v(-4418.08, 1136.1) * mm, "radius": 6.86 * mm});
            skLineSegment(sketch, "E616", {"start": v(-4220.51, 256.04) * mm, "end": v(-4310.31, 166.23) * mm});
            skLineSegment(sketch, "E617", {"start": v(-4310.31, 166.23) * mm, "end": v(-4707, 562.91) * mm});
            skArc(sketch, "E618", {"start": v(-4707, 562.91) * mm, "mid": v(-4628.72, 626.9) * mm, "end": v(-4718.16, 579.76) * mm});
            skLineSegment(sketch, "E619", {"start": v(-4718.16, 579.76) * mm, "end": v(-4836.57, 872.09) * mm});
            skLineSegment(sketch, "E620", {"start": v(-4815.02, 911.12) * mm, "end": v(-4836.57, 872.09) * mm});
            skLineSegment(sketch, "E621", {"start": v(-4013.92, 229.14) * mm, "end": v(-3669.69, 573.37) * mm});
            skCircle(sketch, "E622", {"center": v(-4805.02, 863.7) * mm, "radius": 7.11 * mm});
            skCircle(sketch, "E623", {"center": v(-4705.45, 848.73) * mm, "radius": 6.86 * mm});
            skCircle(sketch, "E624", {"center": v(-4633.6, 920.58) * mm, "radius": 6.86 * mm});
            skCircle(sketch, "E625", {"center": v(-4669.52, 884.65) * mm, "radius": 6.86 * mm});
            skCircle(sketch, "E626", {"center": v(-4741.37, 812.81) * mm, "radius": 6.86 * mm});
            skLineSegment(sketch, "E627", {"start": v(-4317.99, 147.33) * mm, "end": v(-4264.1, 201.22) * mm});
            skLineSegment(sketch, "E628", {"start": v(-4264.1, 201.22) * mm, "end": v(-4246.14, 183.25) * mm});
            skLineSegment(sketch, "E629", {"start": v(-4246.14, 183.25) * mm, "end": v(-4300.03, 129.37) * mm});
            skLineSegment(sketch, "E630", {"start": v(-4300.03, 129.37) * mm, "end": v(-4317.99, 147.33) * mm});
            skLineSegment(sketch, "E631", {"start": v(3306.46, -34.41) * mm, "end": v(3090.56, -34.41) * mm});
            skLineSegment(sketch, "E632", {"start": v(3306.46, -15.36) * mm, "end": v(3090.56, -15.36) * mm});
            skLineSegment(sketch, "E633", {"start": v(3090.56, -75.69) * mm, "end": v(3123, -75.69) * mm});
            skLineSegment(sketch, "E634", {"start": v(3090.56, 76.71) * mm, "end": v(3123, 76.71) * mm});
            skLineSegment(sketch, "E635", {"start": v(3084.2, -94.74) * mm, "end": v(3090.56, -94.74) * mm});
            skLineSegment(sketch, "E636", {"start": v(3084.2, 95.76) * mm, "end": v(3090.56, 95.76) * mm});
            skLineSegment(sketch, "E637", {"start": v(3090.56, 60.84) * mm, "end": v(3217.56, -15.36) * mm});
            skLineSegment(sketch, "E638", {"start": v(3090.56, -94.74) * mm, "end": v(3090.56, 95.76) * mm});
            skLineSegment(sketch, "E639", {"start": v(3084.2, -94.74) * mm, "end": v(3084.2, 95.76) * mm});
            skLineSegment(sketch, "E640", {"start": v(3084.2, -75.69) * mm, "end": v(3051.76, -75.69) * mm});
            skLineSegment(sketch, "E641", {"start": v(3084.2, 76.71) * mm, "end": v(3051.76, 76.71) * mm});
            skLineSegment(sketch, "E642", {"start": v(3306.46, -15.36) * mm, "end": v(3306.46, -34.41) * mm});
            skLineSegment(sketch, "E643", {"start": v(4182.76, -34.16) * mm, "end": v(4398.66, -34.16) * mm});
            skLineSegment(sketch, "E644", {"start": v(4182.76, -15.11) * mm, "end": v(4398.66, -15.11) * mm});
            skLineSegment(sketch, "E645", {"start": v(4398.66, -75.44) * mm, "end": v(4366.21, -75.44) * mm});
            skLineSegment(sketch, "E646", {"start": v(4398.66, 76.96) * mm, "end": v(4366.21, 76.96) * mm});
            skLineSegment(sketch, "E647", {"start": v(4405, -94.49) * mm, "end": v(4398.66, -94.49) * mm});
            skLineSegment(sketch, "E648", {"start": v(4405, 96.01) * mm, "end": v(4398.66, 96.01) * mm});
            skLineSegment(sketch, "E649", {"start": v(4398.66, 61.09) * mm, "end": v(4271.66, -15.11) * mm});
            skLineSegment(sketch, "E650", {"start": v(4398.66, -94.49) * mm, "end": v(4398.66, 96.01) * mm});
            skLineSegment(sketch, "E651", {"start": v(4405, -94.49) * mm, "end": v(4405, 96.01) * mm});
            skLineSegment(sketch, "E652", {"start": v(4405, -75.44) * mm, "end": v(4437.45, -75.44) * mm});
            skLineSegment(sketch, "E653", {"start": v(4405, 76.96) * mm, "end": v(4437.45, 76.96) * mm});
            skLineSegment(sketch, "E654", {"start": v(4182.76, -15.11) * mm, "end": v(4182.76, -34.16) * mm});
            skSolve(sketch);
        }
        {
            var Q0;
            {var subQ0=sQuery(id+"F0.wireOp",EDGE,"E493");Q0=makeQuery(id+"F0.imprint","IMPRINT",FACE,{"disambiguationData":[TD([[makeQuery(id+"F0.imprint","IMPRINT",EDGE,{"derivedFrom":subQ0}),-1.0]])]});}
            var sketch = newSketch(context, id + "F1", { "sketchPlane" : qUnion([Q0])});
            skLineSegment(sketch, "E655.0", {"start": v(5194.97, 792.12) * mm, "end": v(5194.97, -274.68) * mm, "construction": true});
            skLineSegment(sketch, "E656.0", {"start": v(5144.17, 741.32) * mm, "end": v(5144.17, -223.88) * mm, "construction": true});
            skLineSegment(sketch, "E657.0", {"start": v(5194.97, -274.68) * mm, "end": v(4636.66, -274.68) * mm, "construction": true});
            skLineSegment(sketch, "E658.0", {"start": v(5144.17, -223.88) * mm, "end": v(4636.66, -223.88) * mm, "construction": true});
            skLineSegment(sketch, "E659.0", {"start": v(5144.17, -223.88) * mm, "end": v(5194.97, -274.68) * mm, "construction": true});
            skLineSegment(sketch, "E660.0", {"start": v(5194.97, 792.12) * mm, "end": v(5144.17, 741.32) * mm, "construction": true});
            skLineSegment(sketch, "E661.0.2", {"start": v(4636.66, -223.88) * mm, "end": v(4636.66, -274.68) * mm, "construction": true});
            skLineSegment(sketch, "E662.0.1", {"start": v(5194.97, 792.12) * mm, "end": v(4636.66, 792.12) * mm, "construction": true});
            skLineSegment(sketch, "E662.0.2", {"start": v(4636.66, 792.12) * mm, "end": v(4636.66, 741.32) * mm, "construction": true});
            skLineSegment(sketch, "E663", {"start": v(4636.66, 766.72) * mm, "end": v(5169.57, 766.72) * mm});
            skLineSegment(sketch, "E664", {"start": v(5169.57, 766.72) * mm, "end": v(5169.57, -249.28) * mm});
            skLineSegment(sketch, "E665", {"start": v(5169.57, -249.28) * mm, "end": v(4636.66, -249.28) * mm});
            skLineSegment(sketch, "E666.0", {"start": v(4636.66, 741.32) * mm, "end": v(5144.17, 741.32) * mm, "construction": true});
            skSolve(sketch);
        }
        {
            var Q0;
            Q0=qCreatedBy(makeId("Right.planeOp"),FACE);
            var Q1;
            Q1=sQuery(id+"F1.wireOp",VERTEX,"E663.start");
            cPlane(context, id + "F2", {"entities" : qUnion([Q0, Q1]), "cplaneType" : CPlaneType.PLANE_POINT, "offset" : 25.4 * mm, "width" : 152.4 * mm, "height" : 152.4 * mm});
        }
        {
            var Q0;
            Q0=qCreatedBy(id+"F2.planeOp",FACE);
            var sketch = newSketch(context, id + "F3", { "sketchPlane" : qUnion([Q0])});
            skPoint(sketch, "E667.0", {"position": v(0, 766.72) * mm});
            skLineSegment(sketch, "E668.top", {"start": v(12.7, 741.32) * mm, "end": v(-12.7, 741.32) * mm});
            skLineSegment(sketch, "E668.left", {"start": v(12.7, 792.12) * mm, "end": v(12.7, 741.32) * mm});
            skLineSegment(sketch, "E668.right", {"start": v(-12.7, 792.12) * mm, "end": v(-12.7, 741.32) * mm});
            skPoint(sketch, "E669.0", {"position": v(0, 792.12) * mm});
            skPoint(sketch, "E670.0", {"position": v(0, 741.32) * mm});
            skLineSegment(sketch, "E671", {"start": v(-12.7, 792.12) * mm, "end": v(12.7, 792.12) * mm});
            skSolve(sketch);
        }
        {
            var Q0;
            Q0=makeQuery(id+"F3.imprint","IMPRINT",FACE,{"disambiguationData":[TD([[makeQuery(id+"F3.imprint","IMPRINT",EDGE,{"derivedFrom":sQuery(id+"F3.wireOp",EDGE,"E668.top")}),-1.0]])]});
            var Q1;
            Q1=sQuery(id+"F1.wireOp",EDGE,"E663");
            var Q2;
            Q2=sQuery(id+"F1.wireOp",EDGE,"E664");
            var Q3;
            Q3=sQuery(id+"F1.wireOp",EDGE,"E665");
            sweep(context, id + "F4", {"profiles" : qUnion([Q0]), "path" : qUnion([Q1, Q2, Q3])});
        }
        {
            var Q0;
            Q0=makeQuery(id+"F4.opSweep","SWEPT_EDGE",EDGE,{"disambiguationData":[OSD([sQuery(id+"F1.wireOp",EDGE,"E665"),sQuery(id+"F3.wireOp",EDGE,"E668.top"),sQuery(id+"F3.wireOp",EDGE,"E668.left")])]});
            var Q1;
            Q1=makeQuery(id+"F4.opSweep","SWEPT_EDGE",EDGE,{"disambiguationData":[OSD([sQuery(id+"F1.wireOp",EDGE,"E664"),sQuery(id+"F3.wireOp",EDGE,"E668.top"),sQuery(id+"F3.wireOp",EDGE,"E668.left")])]});
            var Q2;
            Q2=makeQuery(id+"F4.opSweep","SWEPT_EDGE",EDGE,{"disambiguationData":[OSD([sQuery(id+"F1.wireOp",EDGE,"E664"),sQuery(id+"F3.wireOp",EDGE,"E668.left"),sQuery(id+"F3.wireOp",EDGE,"E671")])]});
            var Q3;
            Q3=makeQuery(id+"F4.opSweep","SWEPT_EDGE",EDGE,{"disambiguationData":[OSD([sQuery(id+"F1.wireOp",EDGE,"E665"),sQuery(id+"F3.wireOp",EDGE,"E668.left"),sQuery(id+"F3.wireOp",EDGE,"E671")])]});
            var Q4;
            Q4=makeQuery(id+"F4.opSweep","SWEPT_EDGE",EDGE,{"disambiguationData":[OSD([sQuery(id+"F1.wireOp",EDGE,"E665"),sQuery(id+"F3.wireOp",EDGE,"E668.top"),sQuery(id+"F3.wireOp",EDGE,"E668.right")])]});
            var Q5;
            Q5=makeQuery(id+"F4.opSweep","SWEPT_EDGE",EDGE,{"disambiguationData":[OSD([sQuery(id+"F1.wireOp",EDGE,"E664"),sQuery(id+"F3.wireOp",EDGE,"E668.top"),sQuery(id+"F3.wireOp",EDGE,"E668.right")])]});
            var Q6;
            Q6=makeQuery(id+"F4.opSweep","SWEPT_EDGE",EDGE,{"disambiguationData":[OSD([sQuery(id+"F1.wireOp",EDGE,"E663"),sQuery(id+"F3.wireOp",EDGE,"E668.top"),sQuery(id+"F3.wireOp",EDGE,"E668.left")])]});
            var Q7;
            Q7=makeQuery(id+"F4.opSweep","SWEPT_EDGE",EDGE,{"disambiguationData":[OSD([sQuery(id+"F1.wireOp",EDGE,"E663"),sQuery(id+"F3.wireOp",EDGE,"E668.left"),sQuery(id+"F3.wireOp",EDGE,"E671")])]});
            var Q8;
            Q8=makeQuery(id+"F4.opSweep","SWEPT_EDGE",EDGE,{"disambiguationData":[OSD([sQuery(id+"F1.wireOp",EDGE,"E663"),sQuery(id+"F3.wireOp",EDGE,"E668.right"),sQuery(id+"F3.wireOp",EDGE,"E671")])]});
            var Q9;
            Q9=makeQuery(id+"F4.opSweep","SWEPT_EDGE",EDGE,{"disambiguationData":[OSD([sQuery(id+"F1.wireOp",EDGE,"E663"),sQuery(id+"F3.wireOp",EDGE,"E668.top"),sQuery(id+"F3.wireOp",EDGE,"E668.right")])]});
            var Q10;
            Q10=makeQuery(id+"F4.opSweep","SWEPT_EDGE",EDGE,{"disambiguationData":[OSD([sQuery(id+"F1.wireOp",EDGE,"E664"),sQuery(id+"F3.wireOp",EDGE,"E668.right"),sQuery(id+"F3.wireOp",EDGE,"E671")])]});
            var Q11;
            Q11=makeQuery(id+"F4.opSweep","SWEPT_EDGE",EDGE,{"disambiguationData":[OSD([sQuery(id+"F1.wireOp",EDGE,"E665"),sQuery(id+"F3.wireOp",EDGE,"E668.right"),sQuery(id+"F3.wireOp",EDGE,"E671")])]});
            fillet(context, id + "F5", {"entities" : qUnion([Q0, Q1, Q2, Q3, Q4, Q5, Q6, Q7, Q8, Q9, Q10, Q11]), "radius" : 6.35 * mm, "tangentPropagation" : true, "allowEdgeOverflow" : false});
        }
    });
